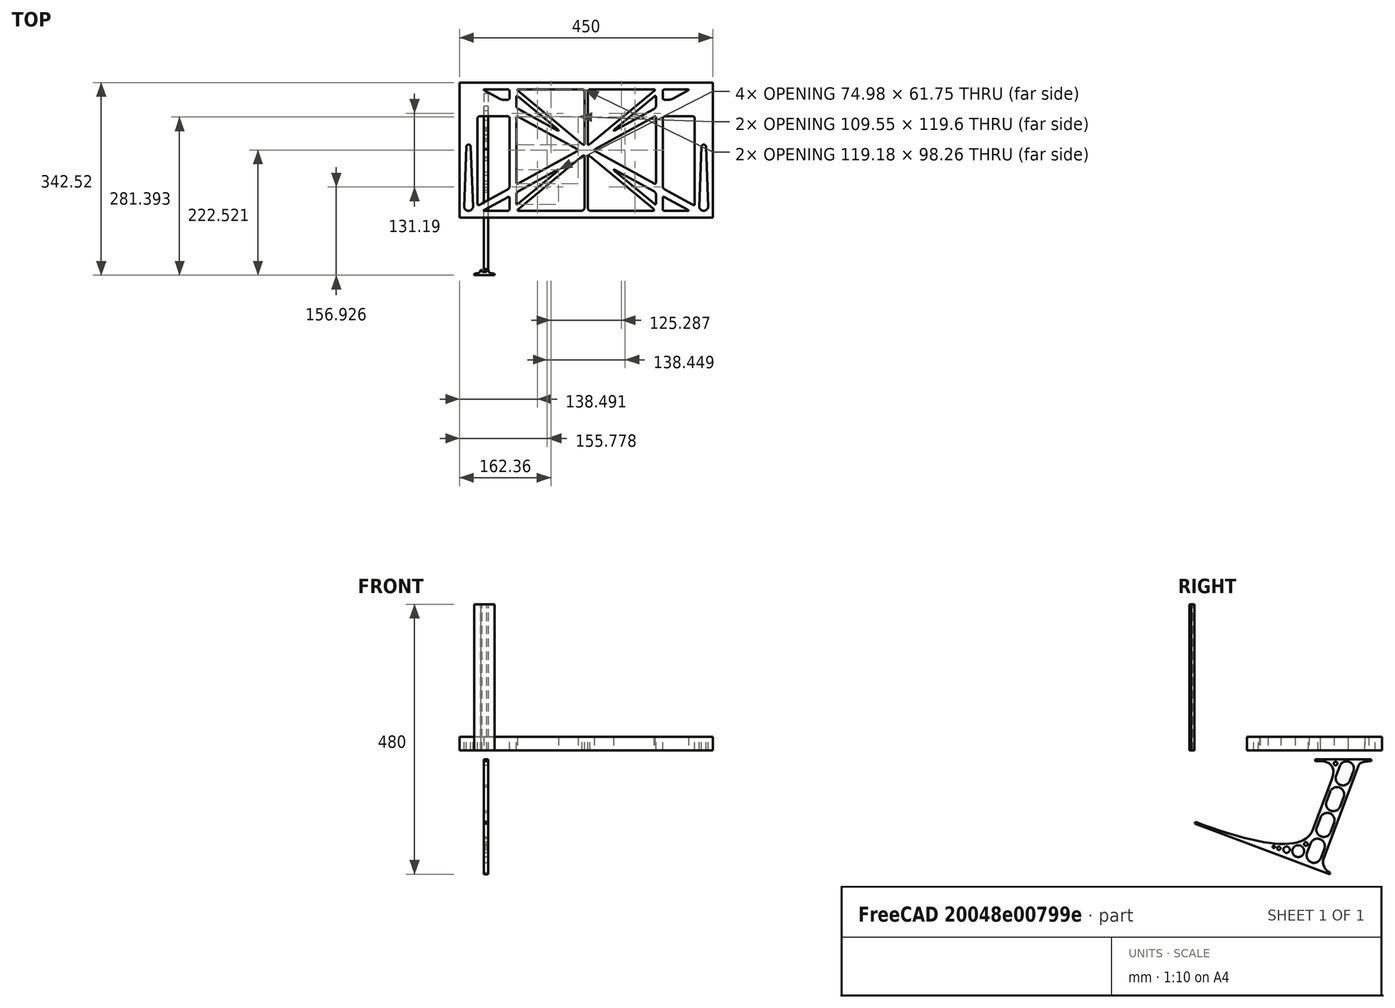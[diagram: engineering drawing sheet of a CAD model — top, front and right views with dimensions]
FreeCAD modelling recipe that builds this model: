
FCSTD DOCUMENT  (FreeCAD 0.19R0.19.2)
Label: laptopStand156FCStd
License: All rights reserved
LicenseURL: http://en.wikipedia.org/wiki/All_rights_reserved
objects: Sketcher::SketchObject×4, Part::Extrusion×3
note: 7 computed .brp shape members not serialized (recipe doc carries the construction recipe); baked Part::Feature solids carry a one-line shape summary decoded from their .brp

FEATURE [Sketcher::SketchObject] Sketch
  FullyConstrained = false
  sketch-geometry (349):
    g0: LineSegment StartX=-10.9272 StartY=-82.7794 StartZ=0 EndX=46.0728 EndY=-51.4823 EndZ=0
    g1: LineSegment StartX=-10.9272 StartY=76.4095 StartZ=0 EndX=-10.9272 EndY=-82.7794 EndZ=0
    g2: LineSegment StartX=46.0728 StartY=76.4095 StartZ=0 EndX=46.0728 EndY=-51.4823 EndZ=0
    g3: LineSegment StartX=-42.9272 StartY=136.221 StartZ=0 EndX=-42.9272 EndY=-103.779 EndZ=0
    g4: LineSegment StartX=407.073 StartY=136.221 StartZ=0 EndX=407.073 EndY=-103.779 EndZ=0
    g5: ArcOfCircle CenterX=-26.9272 CenterY=-83.7794 CenterZ=0 NormalX=0 NormalY=0 NormalZ=1 AngleXU=0 Radius=8 StartAngle=3.14159 EndAngle=6.28319
    g6: ArcOfCircle CenterX=391.073 CenterY=22.1087 CenterZ=0 NormalX=0 NormalY=0 NormalZ=1 AngleXU=0 Radius=8 StartAngle=-4.4e-15 EndAngle=3.14159
    g7: LineSegment StartX=399.073 StartY=22.1087 StartZ=0 EndX=399.073 EndY=-83.7794 EndZ=0
    g8: LineSegment StartX=383.073 StartY=22.1087 StartZ=0 EndX=383.073 EndY=-83.7794 EndZ=0
    g9: ArcOfCircle CenterX=391.073 CenterY=-83.7794 CenterZ=0 NormalX=0 NormalY=0 NormalZ=1 AngleXU=0 Radius=8 StartAngle=3.14159 EndAngle=6.28319
    g10: Circle CenterX=175.022 CenterY=27.0628 CenterZ=0 NormalX=0 NormalY=0 NormalZ=1 AngleXU=0 Radius=1
    g11: Circle CenterX=179.022 CenterY=24.8665 CenterZ=0 NormalX=0 NormalY=0 NormalZ=1 AngleXU=0 Radius=1
    g12: Circle CenterX=179.022 CenterY=27.0628 CenterZ=0 NormalX=0 NormalY=0 NormalZ=1 AngleXU=0 Radius=1
    g13: BSplineCurve PolesCount=3 KnotsCount=2 Degree=2 IsPeriodic=0
    g14: GeomPoint X=175.022 Y=27.0628 Z=0
    g15: GeomPoint X=179.022 Y=27.0628 Z=0
    g16: Circle CenterX=189.124 CenterY=27.0628 CenterZ=0 NormalX=0 NormalY=0 NormalZ=1 AngleXU=0 Radius=1
    g17: Circle CenterX=185.124 CenterY=24.8665 CenterZ=0 NormalX=0 NormalY=0 NormalZ=1 AngleXU=0 Radius=1
    g18: Circle CenterX=185.124 CenterY=27.0628 CenterZ=0 NormalX=0 NormalY=0 NormalZ=1 AngleXU=0 Radius=1
    g19: BSplineCurve PolesCount=3 KnotsCount=2 Degree=2 IsPeriodic=0
    g20: GeomPoint X=189.124 Y=27.0628 Z=0
    g21: GeomPoint X=185.124 Y=27.0628 Z=0
    g22: Circle CenterX=175.022 CenterY=5.37834 CenterZ=0 NormalX=0 NormalY=0 NormalZ=1 AngleXU=0 Radius=1
    g23: Circle CenterX=179.022 CenterY=7.57463 CenterZ=0 NormalX=0 NormalY=0 NormalZ=1 AngleXU=0 Radius=1
    g24: Circle CenterX=179.022 CenterY=5.34704 CenterZ=0 NormalX=0 NormalY=0 NormalZ=1 AngleXU=0 Radius=1
    g25: BSplineCurve PolesCount=3 KnotsCount=2 Degree=2 IsPeriodic=0
    g26: GeomPoint X=175.022 Y=5.37834 Z=0
    g27: GeomPoint X=179.022 Y=5.34704 Z=0
    g28: Circle CenterX=189.124 CenterY=5.37834 CenterZ=0 NormalX=0 NormalY=0 NormalZ=1 AngleXU=0 Radius=1
    g29: Circle CenterX=185.124 CenterY=7.57463 CenterZ=0 NormalX=0 NormalY=0 NormalZ=1 AngleXU=0 Radius=1
    g30: Circle CenterX=185.124 CenterY=5.34704 CenterZ=0 NormalX=0 NormalY=0 NormalZ=1 AngleXU=0 Radius=1
    g31: BSplineCurve PolesCount=3 KnotsCount=2 Degree=2 IsPeriodic=0
    g32: GeomPoint X=189.124 Y=5.37834 Z=0
    g33: GeomPoint X=185.124 Y=5.34704 Z=0
    g34: Circle CenterX=165.871 CenterY=18.1458 CenterZ=0 NormalX=0 NormalY=0 NormalZ=1 AngleXU=0 Radius=1
    g35: Circle CenterX=169.377 CenterY=16.2206 CenterZ=0 NormalX=0 NormalY=0 NormalZ=1 AngleXU=0 Radius=1
    g36: Circle CenterX=165.871 CenterY=14.2954 CenterZ=0 NormalX=0 NormalY=0 NormalZ=1 AngleXU=0 Radius=1
    g37: BSplineCurve PolesCount=3 KnotsCount=2 Degree=2 IsPeriodic=0
    g38: GeomPoint X=165.871 Y=18.1458 Z=0
    g39: GeomPoint X=165.871 Y=14.2954 Z=0
    g40: Circle CenterX=198.275 CenterY=18.1458 CenterZ=0 NormalX=0 NormalY=0 NormalZ=1 AngleXU=0 Radius=1
    g41: Circle CenterX=194.768 CenterY=16.2206 CenterZ=0 NormalX=0 NormalY=0 NormalZ=1 AngleXU=0 Radius=1
    g42: Circle CenterX=198.275 CenterY=14.2954 CenterZ=0 NormalX=0 NormalY=0 NormalZ=1 AngleXU=0 Radius=1
    g43: BSplineCurve PolesCount=3 KnotsCount=2 Degree=2 IsPeriodic=0
    g44: GeomPoint X=198.275 Y=18.1458 Z=0
    g45: GeomPoint X=198.275 Y=14.2954 Z=0
    g46: LineSegment StartX=407.073 StartY=-103.779 StartZ=0 EndX=-42.9272 EndY=-103.779 EndZ=0
    g47: LineSegment StartX=407.073 StartY=136.221 StartZ=0 EndX=-42.9272 EndY=136.221 EndZ=0
    g48: LineSegment StartX=46.0728 StartY=76.4095 StartZ=0 EndX=-10.9272 EndY=76.4095 EndZ=0
    g49: Circle CenterX=125.607 CenterY=54.1951 CenterZ=0 NormalX=0 NormalY=0 NormalZ=1 AngleXU=0 Radius=1
    g50: Circle CenterX=139.632 CenterY=46.4944 CenterZ=0 NormalX=0 NormalY=0 NormalZ=1 AngleXU=0 Radius=1
    g51: Circle CenterX=127.326 CenterY=56.7187 CenterZ=0 NormalX=0 NormalY=0 NormalZ=1 AngleXU=0 Radius=1
    g52: BSplineCurve PolesCount=3 KnotsCount=2 Degree=2 IsPeriodic=0
    g53: GeomPoint X=125.607 Y=54.1951 Z=0
    g54: GeomPoint X=127.326 Y=56.7187 Z=0
    g55: Circle CenterX=236.821 CenterY=56.7187 CenterZ=0 NormalX=0 NormalY=0 NormalZ=1 AngleXU=0 Radius=1
    g56: Circle CenterX=224.513 CenterY=46.4944 CenterZ=0 NormalX=0 NormalY=0 NormalZ=1 AngleXU=0 Radius=1
    g57: Circle CenterX=238.538 CenterY=54.1951 CenterZ=0 NormalX=0 NormalY=0 NormalZ=1 AngleXU=0 Radius=1
    g58: BSplineCurve PolesCount=3 KnotsCount=2 Degree=2 IsPeriodic=0
    g59: GeomPoint X=236.821 Y=56.7187 Z=0
    g60: GeomPoint X=238.538 Y=54.1951 Z=0
    g61: Circle CenterX=238.538 CenterY=-21.7539 CenterZ=0 NormalX=0 NormalY=0 NormalZ=1 AngleXU=0 Radius=1
    g62: Circle CenterX=224.513 CenterY=-14.0532 CenterZ=0 NormalX=0 NormalY=0 NormalZ=1 AngleXU=0 Radius=1
    g63: Circle CenterX=236.821 CenterY=-24.2775 CenterZ=0 NormalX=0 NormalY=0 NormalZ=1 AngleXU=0 Radius=1
    g64: BSplineCurve PolesCount=3 KnotsCount=2 Degree=2 IsPeriodic=0
    g65: GeomPoint X=238.538 Y=-21.7539 Z=0
    g66: GeomPoint X=236.821 Y=-24.2775 Z=0
    g67: Circle CenterX=125.607 CenterY=-21.7539 CenterZ=0 NormalX=0 NormalY=0 NormalZ=1 AngleXU=0 Radius=1
    g68: Circle CenterX=139.632 CenterY=-14.0532 CenterZ=0 NormalX=0 NormalY=0 NormalZ=1 AngleXU=0 Radius=1
    g69: Circle CenterX=127.325 CenterY=-24.2775 CenterZ=0 NormalX=0 NormalY=0 NormalZ=1 AngleXU=0 Radius=1
    g70: BSplineCurve PolesCount=3 KnotsCount=2 Degree=2 IsPeriodic=0
    g71: GeomPoint X=125.607 Y=-21.7539 Z=0
    g72: GeomPoint X=127.325 Y=-24.2775 Z=0
    g73: Circle CenterX=302.996 CenterY=111.695 CenterZ=0 NormalX=0 NormalY=0 NormalZ=1 AngleXU=0 Radius=1
    g74: Circle CenterX=306.073 CenterY=114.251 CenterZ=0 NormalX=0 NormalY=0 NormalZ=1 AngleXU=0 Radius=1
    g75: Circle CenterX=306.073 CenterY=110.251 CenterZ=0 NormalX=0 NormalY=0 NormalZ=1 AngleXU=0 Radius=1
    g76: BSplineCurve PolesCount=3 KnotsCount=2 Degree=2 IsPeriodic=0
    g77: GeomPoint X=302.996 Y=111.695 Z=0
    g78: GeomPoint X=306.073 Y=110.251 Z=0
    g79: Circle CenterX=306.073 CenterY=95.2763 CenterZ=0 NormalX=0 NormalY=0 NormalZ=1 AngleXU=0 Radius=1
    g80: Circle CenterX=306.073 CenterY=91.2763 CenterZ=0 NormalX=0 NormalY=0 NormalZ=1 AngleXU=0 Radius=1
    g81: Circle CenterX=302.567 CenterY=89.3511 CenterZ=0 NormalX=0 NormalY=0 NormalZ=1 AngleXU=0 Radius=1
    g82: BSplineCurve PolesCount=3 KnotsCount=2 Degree=2 IsPeriodic=0
    g83: GeomPoint X=306.073 Y=95.2763 Z=0
    g84: GeomPoint X=302.567 Y=89.3511 Z=0
    g85: LineSegment StartX=306.073 StartY=110.251 StartZ=0 EndX=306.073 EndY=95.2763 EndZ=0
    g86: LineSegment StartX=302.996 StartY=111.695 StartZ=0 EndX=236.821 EndY=56.7187 EndZ=0
    g87: LineSegment StartX=238.538 StartY=54.1951 StartZ=0 EndX=302.567 EndY=89.3511 EndZ=0
    g88: Circle CenterX=61.1496 CenterY=111.695 CenterZ=0 NormalX=0 NormalY=0 NormalZ=1 AngleXU=0 Radius=1
    g89: Circle CenterX=58.0728 CenterY=114.251 CenterZ=0 NormalX=0 NormalY=0 NormalZ=1 AngleXU=0 Radius=1
    g90: Circle CenterX=58.0728 CenterY=110.251 CenterZ=0 NormalX=0 NormalY=0 NormalZ=1 AngleXU=0 Radius=1
    g91: BSplineCurve PolesCount=3 KnotsCount=2 Degree=2 IsPeriodic=0
    g92: GeomPoint X=61.1496 Y=111.695 Z=0
    g93: GeomPoint X=58.0728 Y=110.251 Z=0
    g94: Circle CenterX=61.5791 CenterY=89.3511 CenterZ=0 NormalX=0 NormalY=0 NormalZ=1 AngleXU=0 Radius=1
    g95: Circle CenterX=58.0728 CenterY=91.2763 CenterZ=0 NormalX=0 NormalY=0 NormalZ=1 AngleXU=0 Radius=1
    g96: Circle CenterX=58.0728 CenterY=95.2763 CenterZ=0 NormalX=0 NormalY=0 NormalZ=1 AngleXU=0 Radius=1
    g97: BSplineCurve PolesCount=3 KnotsCount=2 Degree=2 IsPeriodic=0
    g98: GeomPoint X=61.5791 Y=89.3511 Z=0
    g99: GeomPoint X=58.0728 Y=95.2763 Z=0
    g100: LineSegment StartX=58.0728 StartY=110.251 StartZ=0 EndX=58.0728 EndY=95.2763 EndZ=0
    g101: LineSegment StartX=61.1496 StartY=111.695 StartZ=0 EndX=127.326 EndY=56.7187 EndZ=0
    g102: LineSegment StartX=125.607 StartY=54.1951 StartZ=0 EndX=61.5791 EndY=89.3511 EndZ=0
    g103: Circle CenterX=61.5791 CenterY=-56.9099 CenterZ=0 NormalX=0 NormalY=0 NormalZ=1 AngleXU=0 Radius=1
    g104: Circle CenterX=58.0728 CenterY=-58.8351 CenterZ=0 NormalX=0 NormalY=0 NormalZ=1 AngleXU=0 Radius=1
    g105: Circle CenterX=58.0728 CenterY=-62.8351 CenterZ=0 NormalX=0 NormalY=0 NormalZ=1 AngleXU=0 Radius=1
    g106: BSplineCurve PolesCount=3 KnotsCount=2 Degree=2 IsPeriodic=0
    g107: GeomPoint X=61.5791 Y=-56.9099 Z=0
    g108: GeomPoint X=58.0728 Y=-62.8351 Z=0
    g109: Circle CenterX=58.0728 CenterY=-77.8102 CenterZ=0 NormalX=0 NormalY=0 NormalZ=1 AngleXU=0 Radius=1
    g110: Circle CenterX=58.0728 CenterY=-81.8102 CenterZ=0 NormalX=0 NormalY=0 NormalZ=1 AngleXU=0 Radius=1
    g111: Circle CenterX=61.1496 CenterY=-79.2541 CenterZ=0 NormalX=0 NormalY=0 NormalZ=1 AngleXU=0 Radius=1
    g112: BSplineCurve PolesCount=3 KnotsCount=2 Degree=2 IsPeriodic=0
    g113: GeomPoint X=58.0728 Y=-77.8102 Z=0
    g114: GeomPoint X=61.1496 Y=-79.2541 Z=0
    g115: LineSegment StartX=58.0728 StartY=-62.8351 StartZ=0 EndX=58.0728 EndY=-77.8102 EndZ=0
    g116: LineSegment StartX=61.1496 StartY=-79.2541 StartZ=0 EndX=127.325 EndY=-24.2775 EndZ=0
    g117: LineSegment StartX=125.607 StartY=-21.7539 StartZ=0 EndX=61.5791 EndY=-56.9099 EndZ=0
    g118: Circle CenterX=302.567 CenterY=-56.9099 CenterZ=0 NormalX=0 NormalY=0 NormalZ=1 AngleXU=0 Radius=1
    g119: Circle CenterX=306.073 CenterY=-58.8351 CenterZ=0 NormalX=0 NormalY=0 NormalZ=1 AngleXU=0 Radius=1
    g120: Circle CenterX=306.073 CenterY=-62.8351 CenterZ=0 NormalX=0 NormalY=0 NormalZ=1 AngleXU=0 Radius=1
    g121: BSplineCurve PolesCount=3 KnotsCount=2 Degree=2 IsPeriodic=0
    g122: GeomPoint X=302.567 Y=-56.9099 Z=0
    g123: GeomPoint X=306.073 Y=-62.8351 Z=0
    g124: Circle CenterX=302.996 CenterY=-79.2541 CenterZ=0 NormalX=0 NormalY=0 NormalZ=1 AngleXU=0 Radius=1
    g125: Circle CenterX=306.073 CenterY=-81.8102 CenterZ=0 NormalX=0 NormalY=0 NormalZ=1 AngleXU=0 Radius=1
    g126: Circle CenterX=306.073 CenterY=-77.8102 CenterZ=0 NormalX=0 NormalY=0 NormalZ=1 AngleXU=0 Radius=1
    g127: BSplineCurve PolesCount=3 KnotsCount=2 Degree=2 IsPeriodic=0
    g128: GeomPoint X=302.996 Y=-79.2541 Z=0
    g129: GeomPoint X=306.073 Y=-77.8102 Z=0
    g130: LineSegment StartX=306.073 StartY=-62.8351 StartZ=0 EndX=306.073 EndY=-77.8102 EndZ=0
    g131: LineSegment StartX=302.996 StartY=-79.2541 StartZ=0 EndX=236.821 EndY=-24.2775 EndZ=0
    g132: LineSegment StartX=238.538 StartY=-21.7539 StartZ=0 EndX=302.567 EndY=-56.9099 EndZ=0
    g133: Circle CenterX=61.6457 CenterY=-88.8112 CenterZ=0 NormalX=0 NormalY=0 NormalZ=1 AngleXU=0 Radius=1
    g134: Circle CenterX=58.0728 CenterY=-91.7794 CenterZ=0 NormalX=0 NormalY=0 NormalZ=1 AngleXU=0 Radius=1
    g135: Circle CenterX=63.9135 CenterY=-91.7794 CenterZ=0 NormalX=0 NormalY=0 NormalZ=1 AngleXU=0 Radius=1
    g136: BSplineCurve PolesCount=3 KnotsCount=2 Degree=2 IsPeriodic=0
    g137: GeomPoint X=61.6457 Y=-88.8112 Z=0
    g138: GeomPoint X=63.9135 Y=-91.7794 Z=0
    g139: Circle CenterX=179.022 CenterY=-85.8163 CenterZ=0 NormalX=0 NormalY=0 NormalZ=1 AngleXU=0 Radius=1
    g140: Circle CenterX=179.022 CenterY=-91.7794 CenterZ=0 NormalX=0 NormalY=0 NormalZ=1 AngleXU=0 Radius=1
    g141: Circle CenterX=171.895 CenterY=-91.7794 CenterZ=0 NormalX=0 NormalY=0 NormalZ=1 AngleXU=0 Radius=1
    g142: BSplineCurve PolesCount=3 KnotsCount=2 Degree=2 IsPeriodic=0
    g143: GeomPoint X=179.022 Y=-85.8163 Z=0
    g144: GeomPoint X=171.895 Y=-91.7794 Z=0
    g145: Circle CenterX=185.124 CenterY=-86.2028 CenterZ=0 NormalX=0 NormalY=0 NormalZ=1 AngleXU=0 Radius=1
    g146: Circle CenterX=185.124 CenterY=-91.7794 CenterZ=0 NormalX=0 NormalY=0 NormalZ=1 AngleXU=0 Radius=1
    g147: Circle CenterX=191.747 CenterY=-91.7794 CenterZ=0 NormalX=0 NormalY=0 NormalZ=1 AngleXU=0 Radius=1
    g148: BSplineCurve PolesCount=3 KnotsCount=2 Degree=2 IsPeriodic=0
    g149: GeomPoint X=185.124 Y=-86.2028 Z=0
    g150: GeomPoint X=191.747 Y=-91.7794 Z=0
    g151: Circle CenterX=299.888 CenterY=-86.6413 CenterZ=0 NormalX=0 NormalY=0 NormalZ=1 AngleXU=0 Radius=1
    g152: Circle CenterX=306.073 CenterY=-91.7794 CenterZ=0 NormalX=0 NormalY=0 NormalZ=1 AngleXU=0 Radius=1
    g153: Circle CenterX=298.776 CenterY=-91.7794 CenterZ=0 NormalX=0 NormalY=0 NormalZ=1 AngleXU=0 Radius=1
    g154: BSplineCurve PolesCount=3 KnotsCount=2 Degree=2 IsPeriodic=0
    g155: GeomPoint X=299.888 Y=-86.6413 Z=0
    g156: GeomPoint X=298.776 Y=-91.7794 Z=0
    g157: LineSegment StartX=189.124 StartY=5.37834 StartZ=0 EndX=299.888 EndY=-86.6413 EndZ=0
    g158: LineSegment StartX=298.776 StartY=-91.7794 StartZ=0 EndX=191.747 EndY=-91.7794 EndZ=0
    g159: LineSegment StartX=185.124 StartY=-86.2028 StartZ=0 EndX=185.124 EndY=5.34704 EndZ=0
    g160: LineSegment StartX=179.022 StartY=5.34704 StartZ=0 EndX=179.022 EndY=-85.8163 EndZ=0
    g161: LineSegment StartX=171.895 StartY=-91.7794 StartZ=0 EndX=63.9135 EndY=-91.7794 EndZ=0
    g162: LineSegment StartX=61.6457 StartY=-88.8112 StartZ=0 EndX=175.022 EndY=5.37834 EndZ=0
    g163: Circle CenterX=302.073 CenterY=124.221 CenterZ=0 NormalX=0 NormalY=0 NormalZ=1 AngleXU=0 Radius=1
    g164: Circle CenterX=306.073 CenterY=124.221 CenterZ=0 NormalX=0 NormalY=0 NormalZ=1 AngleXU=0 Radius=1
    g165: Circle CenterX=302.996 CenterY=121.665 CenterZ=0 NormalX=0 NormalY=0 NormalZ=1 AngleXU=0 Radius=1
    g166: BSplineCurve PolesCount=3 KnotsCount=2 Degree=2 IsPeriodic=0
    g167: GeomPoint X=302.073 Y=124.221 Z=0
    g168: GeomPoint X=302.996 Y=121.665 Z=0
    g169: Circle CenterX=189.124 CenterY=124.221 CenterZ=0 NormalX=0 NormalY=0 NormalZ=1 AngleXU=0 Radius=1
    g170: Circle CenterX=185.124 CenterY=124.221 CenterZ=0 NormalX=0 NormalY=0 NormalZ=1 AngleXU=0 Radius=1
    g171: Circle CenterX=185.124 CenterY=120.221 CenterZ=0 NormalX=0 NormalY=0 NormalZ=1 AngleXU=0 Radius=1
    g172: BSplineCurve PolesCount=3 KnotsCount=2 Degree=2 IsPeriodic=0
    g173: GeomPoint X=189.124 Y=124.221 Z=0
    g174: GeomPoint X=185.124 Y=120.221 Z=0
    g175: Circle CenterX=175.022 CenterY=124.221 CenterZ=0 NormalX=0 NormalY=0 NormalZ=1 AngleXU=0 Radius=1
    g176: Circle CenterX=179.022 CenterY=124.221 CenterZ=0 NormalX=0 NormalY=0 NormalZ=1 AngleXU=0 Radius=1
    g177: Circle CenterX=179.022 CenterY=120.221 CenterZ=0 NormalX=0 NormalY=0 NormalZ=1 AngleXU=0 Radius=1
    g178: BSplineCurve PolesCount=3 KnotsCount=2 Degree=2 IsPeriodic=0
    g179: GeomPoint X=175.022 Y=124.221 Z=0
    g180: GeomPoint X=179.022 Y=120.221 Z=0
    g181: Circle CenterX=62.0728 CenterY=124.221 CenterZ=0 NormalX=0 NormalY=0 NormalZ=1 AngleXU=0 Radius=1
    g182: Circle CenterX=58.0728 CenterY=124.221 CenterZ=0 NormalX=0 NormalY=0 NormalZ=1 AngleXU=0 Radius=1
    g183: Circle CenterX=61.1496 CenterY=121.665 CenterZ=0 NormalX=0 NormalY=0 NormalZ=1 AngleXU=0 Radius=1
    g184: BSplineCurve PolesCount=3 KnotsCount=2 Degree=2 IsPeriodic=0
    g185: GeomPoint X=62.0728 Y=124.221 Z=0
    g186: GeomPoint X=61.1496 Y=121.665 Z=0
    g187: LineSegment StartX=62.0728 StartY=124.221 StartZ=0 EndX=175.022 EndY=124.221 EndZ=0
    g188: LineSegment StartX=179.022 StartY=120.221 StartZ=0 EndX=179.022 EndY=27.0628 EndZ=0
    g189: LineSegment StartX=185.124 StartY=27.0628 StartZ=0 EndX=185.124 EndY=120.221 EndZ=0
    g190: LineSegment StartX=189.124 StartY=124.221 StartZ=0 EndX=302.073 EndY=124.221 EndZ=0
    g191: LineSegment StartX=302.996 StartY=121.665 StartZ=0 EndX=189.124 EndY=27.0628 EndZ=0
    g192: LineSegment StartX=175.022 StartY=27.0628 StartZ=0 EndX=61.1496 EndY=121.665 EndZ=0
    g193: Circle CenterX=61.5791 CenterY=75.4095 CenterZ=0 NormalX=0 NormalY=0 NormalZ=1 AngleXU=0 Radius=1
    g194: Circle CenterX=58.0728 CenterY=77.3346 CenterZ=0 NormalX=0 NormalY=0 NormalZ=1 AngleXU=0 Radius=1
    g195: Circle CenterX=58.0728 CenterY=73.3346 CenterZ=0 NormalX=0 NormalY=0 NormalZ=1 AngleXU=0 Radius=1
    g196: BSplineCurve PolesCount=3 KnotsCount=2 Degree=2 IsPeriodic=0
    g197: GeomPoint X=61.5791 Y=75.4095 Z=0
    g198: GeomPoint X=58.0728 Y=73.3346 Z=0
    g199: Circle CenterX=58.0728 CenterY=-40.8935 CenterZ=0 NormalX=0 NormalY=0 NormalZ=1 AngleXU=0 Radius=1
    g200: Circle CenterX=58.0728 CenterY=-44.8935 CenterZ=0 NormalX=0 NormalY=0 NormalZ=1 AngleXU=0 Radius=1
    g201: Circle CenterX=61.5791 CenterY=-42.9683 CenterZ=0 NormalX=0 NormalY=0 NormalZ=1 AngleXU=0 Radius=1
    g202: BSplineCurve PolesCount=3 KnotsCount=2 Degree=2 IsPeriodic=0
    g203: GeomPoint X=58.0728 Y=-40.8935 Z=0
    g204: GeomPoint X=61.5791 Y=-42.9683 Z=0
    g205: LineSegment StartX=61.5791 StartY=-42.9683 StartZ=0 EndX=165.871 EndY=14.2954 EndZ=0
    g206: LineSegment StartX=165.871 StartY=18.1458 StartZ=0 EndX=61.5791 EndY=75.4095 EndZ=0
    g207: LineSegment StartX=58.0728 StartY=73.3346 StartZ=0 EndX=58.0728 EndY=-40.8935 EndZ=0
    g208: Circle CenterX=302.567 CenterY=-42.9683 CenterZ=0 NormalX=0 NormalY=0 NormalZ=1 AngleXU=0 Radius=1
    g209: Circle CenterX=306.073 CenterY=-44.8935 CenterZ=0 NormalX=0 NormalY=0 NormalZ=1 AngleXU=0 Radius=1
    g210: Circle CenterX=306.073 CenterY=-40.8935 CenterZ=0 NormalX=0 NormalY=0 NormalZ=1 AngleXU=0 Radius=1
    g211: BSplineCurve PolesCount=3 KnotsCount=2 Degree=2 IsPeriodic=0
    g212: GeomPoint X=302.567 Y=-42.9683 Z=0
    g213: GeomPoint X=306.073 Y=-40.8935 Z=0
    g214: Circle CenterX=306.073 CenterY=73.3346 CenterZ=0 NormalX=0 NormalY=0 NormalZ=1 AngleXU=0 Radius=1
    g215: Circle CenterX=306.073 CenterY=77.3346 CenterZ=0 NormalX=0 NormalY=0 NormalZ=1 AngleXU=0 Radius=1
    g216: Circle CenterX=302.567 CenterY=75.4095 CenterZ=0 NormalX=0 NormalY=0 NormalZ=1 AngleXU=0 Radius=1
    g217: BSplineCurve PolesCount=3 KnotsCount=2 Degree=2 IsPeriodic=0
    g218: GeomPoint X=306.073 Y=73.3346 Z=0
    g219: GeomPoint X=302.567 Y=75.4095 Z=0
    g220: LineSegment StartX=302.567 StartY=-42.9683 StartZ=0 EndX=198.275 EndY=14.2954 EndZ=0
    g221: LineSegment StartX=198.275 StartY=18.1458 StartZ=0 EndX=302.567 EndY=75.4095 EndZ=0
    g222: LineSegment StartX=306.073 StartY=73.3346 StartZ=0 EndX=306.073 EndY=-40.8935 EndZ=0
    g223: LineSegment StartX=322.073 StartY=105.865 StartZ=0 EndX=328.643 EndY=105.865 EndZ=0
    g224: LineSegment StartX=318.073 StartY=120.221 StartZ=0 EndX=318.073 EndY=109.865 EndZ=0
    g225: LineSegment StartX=336.157 StartY=107.779 StartZ=0 EndX=362.567 EndY=122.294 EndZ=0
    g226: Circle CenterX=362.073 CenterY=124.221 CenterZ=0 NormalX=0 NormalY=0 NormalZ=1 AngleXU=0 Radius=1
    g227: Circle CenterX=366.073 CenterY=124.221 CenterZ=0 NormalX=0 NormalY=0 NormalZ=1 AngleXU=0 Radius=1
    g228: Circle CenterX=362.567 CenterY=122.294 CenterZ=0 NormalX=0 NormalY=0 NormalZ=1 AngleXU=0 Radius=1
    g229: BSplineCurve PolesCount=3 KnotsCount=2 Degree=2 IsPeriodic=0
    g230: GeomPoint X=362.073 Y=124.221 Z=0
    g231: GeomPoint X=362.567 Y=122.294 Z=0
    g232: Circle CenterX=322.073 CenterY=124.221 CenterZ=0 NormalX=0 NormalY=0 NormalZ=1 AngleXU=0 Radius=1
    g233: Circle CenterX=318.073 CenterY=124.221 CenterZ=0 NormalX=0 NormalY=0 NormalZ=1 AngleXU=0 Radius=1
    g234: Circle CenterX=318.073 CenterY=120.221 CenterZ=0 NormalX=0 NormalY=0 NormalZ=1 AngleXU=0 Radius=1
    g235: BSplineCurve PolesCount=3 KnotsCount=2 Degree=2 IsPeriodic=0
    g236: GeomPoint X=322.073 Y=124.221 Z=0
    g237: GeomPoint X=318.073 Y=120.221 Z=0
    g238: Circle CenterX=322.073 CenterY=105.865 CenterZ=0 NormalX=0 NormalY=0 NormalZ=1 AngleXU=0 Radius=1
    g239: Circle CenterX=318.073 CenterY=105.865 CenterZ=0 NormalX=0 NormalY=0 NormalZ=1 AngleXU=0 Radius=1
    g240: Circle CenterX=318.073 CenterY=109.865 CenterZ=0 NormalX=0 NormalY=0 NormalZ=1 AngleXU=0 Radius=1
    g241: BSplineCurve PolesCount=3 KnotsCount=2 Degree=2 IsPeriodic=0
    g242: GeomPoint X=322.073 Y=105.865 Z=0
    g243: GeomPoint X=318.073 Y=109.865 Z=0
    g244: Circle CenterX=336.157 CenterY=107.779 CenterZ=0 NormalX=0 NormalY=0 NormalZ=1 AngleXU=0 Radius=1
    g245: Circle CenterX=332.651 CenterY=105.853 CenterZ=0 NormalX=0 NormalY=0 NormalZ=1 AngleXU=0 Radius=1
    g246: Circle CenterX=328.643 CenterY=105.865 CenterZ=0 NormalX=0 NormalY=0 NormalZ=1 AngleXU=0 Radius=1
    g247: BSplineCurve PolesCount=3 KnotsCount=2 Degree=2 IsPeriodic=0
    g248: GeomPoint X=336.157 Y=107.779 Z=0
    g249: GeomPoint X=328.643 Y=105.865 Z=0
    g250: LineSegment StartX=322.073 StartY=124.221 StartZ=0 EndX=362.073 EndY=124.221 EndZ=0
    g251: Circle CenterX=371.567 CenterY=-80.8644 CenterZ=0 NormalX=0 NormalY=0 NormalZ=1 AngleXU=0 Radius=1
    g252: Circle CenterX=375.073 CenterY=-82.7896 CenterZ=0 NormalX=0 NormalY=0 NormalZ=1 AngleXU=0 Radius=1
    g253: Circle CenterX=375.073 CenterY=-78.7896 CenterZ=0 NormalX=0 NormalY=0 NormalZ=1 AngleXU=0 Radius=1
    g254: BSplineCurve PolesCount=3 KnotsCount=2 Degree=2 IsPeriodic=0
    g255: GeomPoint X=371.567 Y=-80.8644 Z=0
    g256: GeomPoint X=375.073 Y=-78.7896 Z=0
    g257: Circle CenterX=321.579 CenterY=-53.4075 CenterZ=0 NormalX=0 NormalY=0 NormalZ=1 AngleXU=0 Radius=1
    g258: Circle CenterX=318.073 CenterY=-51.4823 CenterZ=0 NormalX=0 NormalY=0 NormalZ=1 AngleXU=0 Radius=1
    g259: Circle CenterX=318.073 CenterY=-47.4805 CenterZ=0 NormalX=0 NormalY=0 NormalZ=1 AngleXU=0 Radius=1
    g260: BSplineCurve PolesCount=3 KnotsCount=2 Degree=2 IsPeriodic=0
    g261: GeomPoint X=321.579 Y=-53.4075 Z=0
    g262: GeomPoint X=318.073 Y=-47.4805 Z=0
    g263: LineSegment StartX=371.567 StartY=-80.8644 StartZ=0 EndX=321.579 EndY=-53.4075 EndZ=0
    g264: Circle CenterX=321.579 CenterY=-67.3492 CenterZ=0 NormalX=0 NormalY=0 NormalZ=1 AngleXU=0 Radius=1
    g265: Circle CenterX=318.073 CenterY=-65.424 CenterZ=0 NormalX=0 NormalY=0 NormalZ=1 AngleXU=0 Radius=1
    g266: Circle CenterX=318.073 CenterY=-69.424 CenterZ=0 NormalX=0 NormalY=0 NormalZ=1 AngleXU=0 Radius=1
    g267: BSplineCurve PolesCount=3 KnotsCount=2 Degree=2 IsPeriodic=0
    g268: GeomPoint X=321.579 Y=-67.3492 Z=0
    g269: GeomPoint X=318.073 Y=-69.424 Z=0
    g270: Circle CenterX=362.567 CenterY=-89.8542 CenterZ=0 NormalX=0 NormalY=0 NormalZ=1 AngleXU=0 Radius=1
    g271: Circle CenterX=366.073 CenterY=-91.7794 CenterZ=0 NormalX=0 NormalY=0 NormalZ=1 AngleXU=0 Radius=1
    g272: Circle CenterX=362.073 CenterY=-91.7794 CenterZ=0 NormalX=0 NormalY=0 NormalZ=1 AngleXU=0 Radius=1
    g273: BSplineCurve PolesCount=3 KnotsCount=2 Degree=2 IsPeriodic=0
    g274: GeomPoint X=362.567 Y=-89.8542 Z=0
    g275: GeomPoint X=362.073 Y=-91.7794 Z=0
    g276: Circle CenterX=322.073 CenterY=-91.7794 CenterZ=0 NormalX=0 NormalY=0 NormalZ=1 AngleXU=0 Radius=1
    g277: Circle CenterX=318.073 CenterY=-91.7794 CenterZ=0 NormalX=0 NormalY=0 NormalZ=1 AngleXU=0 Radius=1
    g278: Circle CenterX=318.073 CenterY=-87.7794 CenterZ=0 NormalX=0 NormalY=0 NormalZ=1 AngleXU=0 Radius=1
    g279: BSplineCurve PolesCount=3 KnotsCount=2 Degree=2 IsPeriodic=0
    g280: GeomPoint X=322.073 Y=-91.7794 Z=0
    g281: GeomPoint X=318.073 Y=-87.7794 Z=0
    g282: LineSegment StartX=362.567 StartY=-89.8542 StartZ=0 EndX=321.579 EndY=-67.3492 EndZ=0
    g283: LineSegment StartX=318.073 StartY=-69.424 StartZ=0 EndX=318.073 EndY=-87.7794 EndZ=0
    g284: LineSegment StartX=322.073 StartY=-91.7794 StartZ=0 EndX=362.073 EndY=-91.7794 EndZ=0
    g285: Circle CenterX=2.07281 CenterY=124.221 CenterZ=0 NormalX=0 NormalY=0 NormalZ=1 AngleXU=0 Radius=1
    g286: Circle CenterX=1.57905 CenterY=122.295 CenterZ=0 NormalX=0 NormalY=0 NormalZ=1 AngleXU=0 Radius=1
    g287: BSplineCurve PolesCount=3 KnotsCount=2 Degree=2 IsPeriodic=0
    g288: GeomPoint X=2.07281 Y=124.221 Z=0
    g289: GeomPoint X=1.57905 Y=122.295 Z=0
    g290: Circle CenterX=42.0728 CenterY=124.221 CenterZ=0 NormalX=0 NormalY=0 NormalZ=1 AngleXU=0 Radius=1
    g291: Circle CenterX=46.0728 CenterY=124.221 CenterZ=0 NormalX=0 NormalY=0 NormalZ=1 AngleXU=0 Radius=1
    g292: Circle CenterX=46.0728 CenterY=120.221 CenterZ=0 NormalX=0 NormalY=0 NormalZ=1 AngleXU=0 Radius=1
    g293: BSplineCurve PolesCount=3 KnotsCount=2 Degree=2 IsPeriodic=0
    g294: GeomPoint X=42.0728 Y=124.221 Z=0
    g295: GeomPoint X=46.0728 Y=120.221 Z=0
    g296: Circle CenterX=46.0728 CenterY=109.865 CenterZ=0 NormalX=0 NormalY=0 NormalZ=1 AngleXU=0 Radius=1
    g297: Circle CenterX=46.0728 CenterY=105.865 CenterZ=0 NormalX=0 NormalY=0 NormalZ=1 AngleXU=0 Radius=1
    g298: Circle CenterX=42.0728 CenterY=105.865 CenterZ=0 NormalX=0 NormalY=0 NormalZ=1 AngleXU=0 Radius=1
    g299: BSplineCurve PolesCount=3 KnotsCount=2 Degree=2 IsPeriodic=0
    g300: GeomPoint X=46.0728 Y=109.865 Z=0
    g301: GeomPoint X=42.0728 Y=105.865 Z=0
    g302: Circle CenterX=35.5028 CenterY=105.865 CenterZ=0 NormalX=0 NormalY=0 NormalZ=1 AngleXU=0 Radius=1
    g303: Circle CenterX=31.5028 CenterY=105.865 CenterZ=0 NormalX=0 NormalY=0 NormalZ=1 AngleXU=0 Radius=1
    g304: Circle CenterX=27.9965 CenterY=107.79 CenterZ=0 NormalX=0 NormalY=0 NormalZ=1 AngleXU=0 Radius=1
    g305: BSplineCurve PolesCount=3 KnotsCount=2 Degree=2 IsPeriodic=0
    g306: GeomPoint X=35.5028 Y=105.865 Z=0
    g307: GeomPoint X=27.9965 Y=107.79 Z=0
    g308: LineSegment StartX=2.07281 StartY=124.221 StartZ=0 EndX=42.0728 EndY=124.221 EndZ=0
    g309: LineSegment StartX=46.0728 StartY=120.221 StartZ=0 EndX=46.0728 EndY=109.865 EndZ=0
    g310: LineSegment StartX=42.0728 StartY=105.865 StartZ=0 EndX=35.5028 EndY=105.865 EndZ=0
    g311: LineSegment StartX=27.9965 StartY=107.79 StartZ=0 EndX=1.57905 EndY=122.295 EndZ=0
    g312: Circle CenterX=42.5666 CenterY=-67.3492 CenterZ=0 NormalX=0 NormalY=0 NormalZ=1 AngleXU=0 Radius=1
    g313: Circle CenterX=46.0728 CenterY=-65.424 CenterZ=0 NormalX=0 NormalY=0 NormalZ=1 AngleXU=0 Radius=1
    g314: Circle CenterX=46.0728 CenterY=-69.424 CenterZ=0 NormalX=0 NormalY=0 NormalZ=1 AngleXU=0 Radius=1
    g315: BSplineCurve PolesCount=3 KnotsCount=2 Degree=2 IsPeriodic=0
    g316: GeomPoint X=42.5666 Y=-67.3492 Z=0
    g317: GeomPoint X=46.0728 Y=-69.424 Z=0
    g318: Circle CenterX=46.0728 CenterY=-87.7794 CenterZ=0 NormalX=0 NormalY=0 NormalZ=1 AngleXU=0 Radius=1
    g319: Circle CenterX=46.0728 CenterY=-91.7794 CenterZ=0 NormalX=0 NormalY=0 NormalZ=1 AngleXU=0 Radius=1
    g320: Circle CenterX=42.0728 CenterY=-91.7794 CenterZ=0 NormalX=0 NormalY=0 NormalZ=1 AngleXU=0 Radius=1
    g321: BSplineCurve PolesCount=3 KnotsCount=2 Degree=2 IsPeriodic=0
    g322: GeomPoint X=46.0728 Y=-87.7794 Z=0
    g323: GeomPoint X=42.0728 Y=-91.7794 Z=0
    g324: Circle CenterX=2.07281 CenterY=-91.7794 CenterZ=0 NormalX=0 NormalY=0 NormalZ=1 AngleXU=0 Radius=1
    g325: Circle CenterX=-1.92719 CenterY=-91.7794 CenterZ=0 NormalX=0 NormalY=0 NormalZ=1 AngleXU=0 Radius=1
    g326: Circle CenterX=1.57905 CenterY=-89.8542 CenterZ=0 NormalX=0 NormalY=0 NormalZ=1 AngleXU=0 Radius=1
    g327: BSplineCurve PolesCount=3 KnotsCount=2 Degree=2 IsPeriodic=0
    g328: GeomPoint X=2.07281 Y=-91.7794 Z=0
    g329: GeomPoint X=1.57905 Y=-89.8542 Z=0
    g330: LineSegment StartX=2.07281 StartY=-91.7794 StartZ=0 EndX=42.0728 EndY=-91.7794 EndZ=0
    g331: LineSegment StartX=46.0728 StartY=-87.7794 StartZ=0 EndX=46.0728 EndY=-69.424 EndZ=0
    g332: LineSegment StartX=42.5666 StartY=-67.3492 StartZ=0 EndX=1.57905 EndY=-89.8542 EndZ=0
    g333: Circle CenterX=322.073 CenterY=76.4095 CenterZ=0 NormalX=0 NormalY=0 NormalZ=1 AngleXU=0 Radius=4
    g334: BSplineCurve PolesCount=3 KnotsCount=2 Degree=2 IsPeriodic=0
    g335: GeomPoint X=318.073 Y=72.4095 Z=0
    g336: GeomPoint X=322.073 Y=76.4095 Z=0
    g337: Circle CenterX=375.073 CenterY=72.4095 CenterZ=0 NormalX=0 NormalY=0 NormalZ=1 AngleXU=0 Radius=1
    g338: Circle CenterX=375.073 CenterY=76.4095 CenterZ=0 NormalX=0 NormalY=0 NormalZ=1 AngleXU=0 Radius=1
    g339: Circle CenterX=371.073 CenterY=76.4095 CenterZ=0 NormalX=0 NormalY=0 NormalZ=1 AngleXU=0 Radius=1
    g340: BSplineCurve PolesCount=3 KnotsCount=2 Degree=2 IsPeriodic=0
    g341: GeomPoint X=375.073 Y=72.4095 Z=0
    g342: GeomPoint X=371.073 Y=76.4095 Z=0
    g343: LineSegment StartX=322.073 StartY=76.4095 StartZ=0 EndX=371.073 EndY=76.4095 EndZ=0
    g344: LineSegment StartX=318.073 StartY=72.4095 StartZ=0 EndX=318.073 EndY=-47.4805 EndZ=0
    g345: LineSegment StartX=375.073 StartY=72.4095 StartZ=0 EndX=375.073 EndY=-78.7896 EndZ=0
    g346: ArcOfCircle CenterX=-26.9272 CenterY=22.1087 CenterZ=0 NormalX=0 NormalY=0 NormalZ=1 AngleXU=0 Radius=4 StartAngle=5e-16 EndAngle=3.14159
    g347: LineSegment StartX=-30.9272 StartY=22.1087 StartZ=0 EndX=-34.9272 EndY=-83.7794 EndZ=0
    g348: LineSegment StartX=-18.9272 StartY=-83.7794 StartZ=0 EndX=-22.9272 EndY=22.1087 EndZ=0
  constraints (572):
    c: Coincident(g0,g2)
    c: Block(g0)
    c: Block(g1)
    c: Vertical(g3)
    c: Vertical(g4)
    c: Block(g4)
    c: Block(g3)
    c: Tangent(g6,g7) = 1.5708
    c: Tangent(g7,g9) = 1.5708
    c: Equal(g6,g9)
    c: Coincident(g8,g6)
    c: Coincident(g8,g9)
    c: Block(g7)
    c: Block(g8)
    c: Weight(g10) = 1
    c: Equal(g10,g11)
    c: Equal(g10,g12)
    c: InternalAlignment(g10,g13)
    c: InternalAlignment(g11,g13)
    c: InternalAlignment(g12,g13)
    c: InternalAlignment(g14,g13)
    c: InternalAlignment(g15,g13)
    c: Weight(g16) = 1
    c: Equal(g16,g17)
    c: Equal(g16,g18)
    c: InternalAlignment(g16,g19)
    c: InternalAlignment(g17,g19)
    c: InternalAlignment(g18,g19)
    c: InternalAlignment(g20,g19)
    c: InternalAlignment(g21,g19)
    c: Block(g19)
    c: Block(g13)
    c: Weight(g22) = 1
    c: Equal(g22,g23)
    c: Equal(g22,g24)
    c: InternalAlignment(g22,g25)
    c: InternalAlignment(g23,g25)
    c: InternalAlignment(g24,g25)
    c: InternalAlignment(g26,g25)
    c: InternalAlignment(g27,g25)
    c: Weight(g28) = 1
    c: Equal(g28,g29)
    c: Equal(g28,g30)
    c: InternalAlignment(g28,g31)
    c: InternalAlignment(g29,g31)
    c: InternalAlignment(g30,g31)
    c: InternalAlignment(g32,g31)
    c: InternalAlignment(g33,g31)
    c: Block(g31)
    c: Block(g25)
    c: Weight(g34) = 1
    c: Equal(g34,g35)
    c: Equal(g34,g36)
    c: InternalAlignment(g34,g37)
    c: InternalAlignment(g35,g37)
    c: InternalAlignment(g36,g37)
    c: InternalAlignment(g38,g37)
    c: InternalAlignment(g39,g37)
    c: Weight(g40) = 1
    c: Equal(g40,g41)
    c: Equal(g40,g42)
    c: InternalAlignment(g40,g43)
    c: InternalAlignment(g41,g43)
    c: InternalAlignment(g42,g43)
    c: InternalAlignment(g44,g43)
    c: InternalAlignment(g45,g43)
    c: Block(g37)
    c: Block(g43)
    c: Coincident(g46,g4)
    c: Coincident(g46,g3)
    c: Horizontal(g46)
    c: Distance(g46) = 450
    c: Coincident(g47,g4)
    c: Coincident(g47,g3)
    c: Horizontal(g47)
    c: Horizontal(g48)
    c: Coincident(g2,g48)
    c: Block(g48)
    c: Coincident(g1,g48)
    c: Weight(g49) = 1
    c: Equal(g49,g50)
    c: Equal(g49,g51)
    c: InternalAlignment(g49,g52)
    c: InternalAlignment(g50,g52)
    c: InternalAlignment(g51,g52)
    c: InternalAlignment(g53,g52)
    c: InternalAlignment(g54,g52)
    c: Block(g52)
    c: Weight(g55) = 1
    c: Equal(g55,g56)
    c: Equal(g55,g57)
    c: InternalAlignment(g55,g58)
    c: InternalAlignment(g56,g58)
    c: InternalAlignment(g57,g58)
    c: InternalAlignment(g59,g58)
    c: InternalAlignment(g60,g58)
    c: Block(g58)
    c: Weight(g61) = 1
    c: Equal(g61,g62)
    c: Equal(g61,g63)
    c: InternalAlignment(g61,g64)
    c: InternalAlignment(g62,g64)
    c: InternalAlignment(g63,g64)
    c: InternalAlignment(g65,g64)
    c: InternalAlignment(g66,g64)
    c: Block(g64)
    c: Weight(g67) = 1
    c: Equal(g67,g68)
    c: Equal(g67,g69)
    c: InternalAlignment(g67,g70)
    c: InternalAlignment(g68,g70)
    c: InternalAlignment(g69,g70)
    c: InternalAlignment(g71,g70)
    c: InternalAlignment(g72,g70)
    c: Block(g70)
    c: Weight(g73) = 1
    c: Equal(g73,g74)
    c: Equal(g73,g75)
    c: InternalAlignment(g73,g76)
    c: InternalAlignment(g74,g76)
    c: InternalAlignment(g75,g76)
    c: InternalAlignment(g77,g76)
    c: InternalAlignment(g78,g76)
    c: Weight(g79) = 1
    c: Equal(g79,g80)
    c: Equal(g79,g81)
    c: InternalAlignment(g79,g82)
    c: InternalAlignment(g80,g82)
    c: InternalAlignment(g81,g82)
    c: InternalAlignment(g83,g82)
    c: InternalAlignment(g84,g82)
    c: Block(g76)
    c: Block(g82)
    c: Coincident(g85,g76)
    c: Coincident(g85,g82)
    c: Vertical(g85)
    c: Coincident(g86,g76)
    c: Coincident(g86,g58)
    c: Coincident(g87,g58)
    c: Coincident(g87,g82)
    c: Weight(g88) = 1
    c: Equal(g88,g89)
    c: Equal(g88,g90)
    c: InternalAlignment(g88,g91)
    c: InternalAlignment(g89,g91)
    c: InternalAlignment(g90,g91)
    c: InternalAlignment(g92,g91)
    c: InternalAlignment(g93,g91)
    c: Weight(g94) = 1
    c: Equal(g94,g95)
    c: Equal(g94,g96)
    c: InternalAlignment(g94,g97)
    c: InternalAlignment(g95,g97)
    c: InternalAlignment(g96,g97)
    c: InternalAlignment(g98,g97)
    c: InternalAlignment(g99,g97)
    c: Block(g91)
    c: Block(g97)
    c: Coincident(g100,g91)
    c: Coincident(g100,g97)
    c: Vertical(g100)
    c: Coincident(g101,g91)
    c: Coincident(g101,g52)
    c: Coincident(g102,g52)
    c: Coincident(g102,g97)
    c: Weight(g103) = 1
    c: Equal(g103,g104)
    c: Equal(g103,g105)
    c: InternalAlignment(g103,g106)
    c: InternalAlignment(g104,g106)
    c: InternalAlignment(g105,g106)
    c: InternalAlignment(g107,g106)
    c: InternalAlignment(g108,g106)
    c: Weight(g109) = 1
    c: Equal(g109,g110)
    c: Equal(g109,g111)
    c: InternalAlignment(g109,g112)
    c: InternalAlignment(g110,g112)
    c: InternalAlignment(g111,g112)
    c: InternalAlignment(g113,g112)
    c: InternalAlignment(g114,g112)
    c: Block(g106)
    c: Block(g112)
    c: Coincident(g115,g106)
    c: Coincident(g115,g112)
    c: Vertical(g115)
    c: Coincident(g116,g112)
    c: Coincident(g116,g70)
    c: Coincident(g117,g70)
    c: Coincident(g117,g106)
    c: Weight(g118) = 1
    c: Equal(g118,g119)
    c: Equal(g118,g120)
    c: InternalAlignment(g118,g121)
    c: InternalAlignment(g119,g121)
    c: InternalAlignment(g120,g121)
    c: InternalAlignment(g122,g121)
    c: InternalAlignment(g123,g121)
    c: Weight(g124) = 1
    c: Equal(g124,g125)
    c: Equal(g124,g126)
    c: InternalAlignment(g124,g127)
    c: InternalAlignment(g125,g127)
    c: InternalAlignment(g126,g127)
    c: InternalAlignment(g128,g127)
    c: InternalAlignment(g129,g127)
    c: Block(g121)
    c: Block(g127)
    c: Coincident(g130,g121)
    c: Coincident(g130,g127)
    c: Vertical(g130)
    c: Coincident(g131,g127)
    c: Coincident(g131,g64)
    c: Coincident(g132,g64)
    c: Coincident(g132,g121)
    c: Weight(g133) = 1
    c: Equal(g133,g134)
    c: Equal(g133,g135)
    c: InternalAlignment(g133,g136)
    c: InternalAlignment(g134,g136)
    c: InternalAlignment(g135,g136)
    c: InternalAlignment(g137,g136)
    c: InternalAlignment(g138,g136)
    c: Weight(g139) = 1
    c: Equal(g139,g140)
    c: Equal(g139,g141)
    c: InternalAlignment(g139,g142)
    c: InternalAlignment(g140,g142)
    c: InternalAlignment(g141,g142)
    c: InternalAlignment(g143,g142)
    c: InternalAlignment(g144,g142)
    c: Weight(g145) = 1
    c: Equal(g145,g146)
    c: Equal(g145,g147)
    c: InternalAlignment(g145,g148)
    c: InternalAlignment(g146,g148)
    c: InternalAlignment(g147,g148)
    c: InternalAlignment(g149,g148)
    c: InternalAlignment(g150,g148)
    c: Weight(g151) = 1
    c: Equal(g151,g152)
    c: Equal(g151,g153)
    c: InternalAlignment(g151,g154)
    c: InternalAlignment(g152,g154)
    c: InternalAlignment(g153,g154)
    c: InternalAlignment(g155,g154)
    c: InternalAlignment(g156,g154)
    c: Block(g154)
    c: Block(g148)
    c: Block(g142)
    c: Block(g136)
    c: Coincident(g157,g31)
    c: Coincident(g157,g154)
    c: Coincident(g158,g154)
    c: Coincident(g158,g148)
    c: Horizontal(g158)
    c: Coincident(g159,g148)
    c: Coincident(g159,g31)
    c: Vertical(g159)
    c: Coincident(g160,g25)
    c: Coincident(g160,g142)
    c: Vertical(g160)
    c: Coincident(g161,g142)
    c: Coincident(g161,g136)
    c: Horizontal(g161)
    c: Coincident(g162,g136)
    c: Coincident(g162,g25)
    c: Weight(g163) = 1
    c: Equal(g163,g164)
    c: Equal(g163,g165)
    c: InternalAlignment(g163,g166)
    c: InternalAlignment(g164,g166)
    c: InternalAlignment(g165,g166)
    c: InternalAlignment(g167,g166)
    c: InternalAlignment(g168,g166)
    c: Weight(g169) = 1
    c: Equal(g169,g170)
    c: Equal(g169,g171)
    c: InternalAlignment(g169,g172)
    c: InternalAlignment(g170,g172)
    c: InternalAlignment(g171,g172)
    c: InternalAlignment(g173,g172)
    c: InternalAlignment(g174,g172)
    c: Weight(g175) = 1
    c: Equal(g175,g176)
    c: Equal(g175,g177)
    c: InternalAlignment(g175,g178)
    c: InternalAlignment(g176,g178)
    c: InternalAlignment(g177,g178)
    c: InternalAlignment(g179,g178)
    c: InternalAlignment(g180,g178)
    c: Weight(g181) = 1
    c: Equal(g181,g182)
    c: Equal(g181,g183)
    c: InternalAlignment(g181,g184)
    c: InternalAlignment(g182,g184)
    c: InternalAlignment(g183,g184)
    c: InternalAlignment(g185,g184)
    c: InternalAlignment(g186,g184)
    c: Block(g184)
    c: Block(g178)
    c: Block(g172)
    c: Block(g166)
    c: Coincident(g187,g184)
    c: Coincident(g187,g178)
    c: Horizontal(g187)
    c: Coincident(g188,g178)
    c: Coincident(g188,g13)
    c: Vertical(g188)
    c: Coincident(g189,g19)
    c: Coincident(g189,g172)
    c: Vertical(g189)
    c: Coincident(g190,g172)
    c: Coincident(g190,g166)
    c: Horizontal(g190)
    c: Coincident(g191,g166)
    c: Coincident(g191,g19)
    c: Coincident(g192,g13)
    c: Weight(g193) = 1
    c: Equal(g193,g194)
    c: Equal(g193,g195)
    c: InternalAlignment(g193,g196)
    c: InternalAlignment(g194,g196)
    c: InternalAlignment(g195,g196)
    c: InternalAlignment(g197,g196)
    c: InternalAlignment(g198,g196)
    c: Weight(g199) = 1
    c: Equal(g199,g200)
    c: Equal(g199,g201)
    c: InternalAlignment(g199,g202)
    c: InternalAlignment(g200,g202)
    c: InternalAlignment(g201,g202)
    c: InternalAlignment(g203,g202)
    c: InternalAlignment(g204,g202)
    c: Block(g202)
    c: Block(g196)
    c: Coincident(g205,g202)
    c: Coincident(g205,g37)
    c: Coincident(g206,g37)
    c: Coincident(g206,g196)
    c: Coincident(g207,g196)
    c: Coincident(g207,g202)
    c: Vertical(g207)
    c: Weight(g208) = 1
    c: Equal(g208,g209)
    c: Equal(g208,g210)
    c: InternalAlignment(g208,g211)
    c: InternalAlignment(g209,g211)
    c: InternalAlignment(g210,g211)
    c: InternalAlignment(g212,g211)
    c: InternalAlignment(g213,g211)
    c: Weight(g214) = 1
    c: Equal(g214,g215)
    c: Equal(g214,g216)
    c: InternalAlignment(g214,g217)
    c: InternalAlignment(g215,g217)
    c: InternalAlignment(g216,g217)
    c: InternalAlignment(g218,g217)
    c: InternalAlignment(g219,g217)
    c: Block(g217)
    c: Block(g211)
    c: Coincident(g220,g211)
    c: Coincident(g220,g43)
    c: Coincident(g221,g43)
    c: Coincident(g221,g217)
    c: Coincident(g222,g217)
    c: Coincident(g222,g211)
    c: Vertical(g222)
    c: Horizontal(g223)
    c: Block(g223)
    c: Vertical(g224)
    c: Block(g224)
    c: Block(g225)
    c: Weight(g226) = 1
    c: Equal(g226,g227)
    c: Equal(g226,g228)
    c: InternalAlignment(g226,g229)
    c: InternalAlignment(g227,g229)
    c: InternalAlignment(g228,g229)
    c: InternalAlignment(g230,g229)
    c: InternalAlignment(g231,g229)
    c: Weight(g232) = 1
    c: Equal(g232,g233)
    c: Equal(g232,g234)
    c: InternalAlignment(g232,g235)
    c: InternalAlignment(g233,g235)
    c: InternalAlignment(g234,g235)
    c: InternalAlignment(g236,g235)
    c: InternalAlignment(g237,g235)
    c: Weight(g238) = 1
    c: Equal(g238,g239)
    c: Equal(g238,g240)
    c: InternalAlignment(g238,g241)
    c: InternalAlignment(g239,g241)
    c: InternalAlignment(g240,g241)
    c: InternalAlignment(g242,g241)
    c: InternalAlignment(g243,g241)
    c: Weight(g244) = 1
    c: Equal(g244,g245)
    c: Equal(g244,g246)
    c: InternalAlignment(g244,g247)
    c: InternalAlignment(g245,g247)
    c: InternalAlignment(g246,g247)
    c: InternalAlignment(g248,g247)
    c: InternalAlignment(g249,g247)
    c: Block(g229)
    c: Block(g235)
    c: Block(g241)
    c: Block(g247)
    c: Coincident(g250,g235)
    c: Coincident(g250,g229)
    c: Horizontal(g250)
    c: Block(g192)
    c: Weight(g251) = 1
    c: Equal(g251,g252)
    c: Equal(g251,g253)
    c: InternalAlignment(g251,g254)
    c: InternalAlignment(g252,g254)
    c: InternalAlignment(g253,g254)
    c: InternalAlignment(g255,g254)
    c: InternalAlignment(g256,g254)
    c: Weight(g257) = 1
    c: Equal(g257,g258)
    c: Equal(g257,g259)
    c: InternalAlignment(g257,g260)
    c: InternalAlignment(g258,g260)
    c: InternalAlignment(g259,g260)
    c: InternalAlignment(g261,g260)
    c: InternalAlignment(g262,g260)
    c: Block(g254)
    c: Block(g260)
    c: Coincident(g263,g254)
    c: Coincident(g263,g260)
    c: Weight(g264) = 1
    c: Equal(g264,g265)
    c: Equal(g264,g266)
    c: InternalAlignment(g264,g267)
    c: InternalAlignment(g265,g267)
    c: InternalAlignment(g266,g267)
    c: InternalAlignment(g268,g267)
    c: InternalAlignment(g269,g267)
    c: Weight(g270) = 1
    c: Equal(g270,g271)
    c: Equal(g270,g272)
    c: InternalAlignment(g270,g273)
    c: InternalAlignment(g271,g273)
    c: InternalAlignment(g272,g273)
    c: InternalAlignment(g274,g273)
    c: InternalAlignment(g275,g273)
    c: Weight(g276) = 1
    c: Equal(g276,g277)
    c: Equal(g276,g278)
    c: InternalAlignment(g276,g279)
    c: InternalAlignment(g277,g279)
    c: InternalAlignment(g278,g279)
    c: InternalAlignment(g280,g279)
    c: InternalAlignment(g281,g279)
    c: Block(g279)
    c: Block(g273)
    c: Block(g267)
    c: Coincident(g282,g273)
    c: Coincident(g282,g267)
    c: Coincident(g283,g267)
    c: Coincident(g283,g279)
    c: Vertical(g283)
    c: Coincident(g284,g279)
    c: Coincident(g284,g273)
    c: Horizontal(g284)
    c: Weight(g285) = 1
    c: Equal(g285,g286)
    c: InternalAlignment(g285,g287)
    c: InternalAlignment(g286,g287)
    c: InternalAlignment(g288,g287)
    c: InternalAlignment(g289,g287)
    c: Weight(g290) = 1
    c: InternalAlignment(g291,g293)
    c: InternalAlignment(g292,g293)
    c: InternalAlignment(g294,g293)
    c: InternalAlignment(g295,g293)
    c: Weight(g296) = 1
    c: Equal(g296,g297)
    c: Equal(g296,g298)
    c: InternalAlignment(g296,g299)
    c: InternalAlignment(g297,g299)
    c: InternalAlignment(g298,g299)
    c: InternalAlignment(g300,g299)
    c: InternalAlignment(g301,g299)
    c: Equal(g302,g303)
    c: Equal(g302,g304)
    c: InternalAlignment(g302,g305)
    c: InternalAlignment(g303,g305)
    c: InternalAlignment(g304,g305)
    c: InternalAlignment(g306,g305)
    c: InternalAlignment(g307,g305)
    c: Block(g293)
    c: Block(g299)
    c: Block(g305)
    c: Block(g287)
    c: Coincident(g308,g287)
    c: Coincident(g308,g293)
    c: Horizontal(g308)
    c: Coincident(g309,g293)
    c: Coincident(g309,g299)
    c: Vertical(g309)
    c: Coincident(g310,g299)
    c: Coincident(g310,g305)
    c: Horizontal(g310)
    c: Coincident(g311,g305)
    c: Coincident(g311,g287)
    c: Weight(g312) = 1
    c: Equal(g312,g313)
    c: Equal(g312,g314)
    c: InternalAlignment(g312,g315)
    c: InternalAlignment(g313,g315)
    c: InternalAlignment(g314,g315)
    c: InternalAlignment(g316,g315)
    c: InternalAlignment(g317,g315)
    c: Weight(g318) = 1
    c: Equal(g318,g319)
    c: Equal(g318,g320)
    c: InternalAlignment(g318,g321)
    c: InternalAlignment(g319,g321)
    c: InternalAlignment(g320,g321)
    c: InternalAlignment(g322,g321)
    c: InternalAlignment(g323,g321)
    c: Weight(g324) = 1
    c: Equal(g324,g325)
    c: Equal(g324,g326)
    c: InternalAlignment(g324,g327)
    c: InternalAlignment(g325,g327)
    c: InternalAlignment(g326,g327)
    c: InternalAlignment(g328,g327)
    c: InternalAlignment(g329,g327)
    c: Block(g327)
    c: Block(g321)
    c: Block(g315)
    c: Coincident(g330,g327)
    c: Coincident(g330,g321)
    c: Horizontal(g330)
    c: Coincident(g331,g321)
    c: Coincident(g331,g315)
    c: Vertical(g331)
    c: Coincident(g332,g315)
    c: Coincident(g332,g327)
    c: InternalAlignment(g333,g334)
    c: InternalAlignment(g335,g334)
    c: InternalAlignment(g336,g334)
    c: Block(g334)
    c: Equal(g337,g338)
    c: Equal(g337,g339)
    c: InternalAlignment(g337,g340)
    c: InternalAlignment(g338,g340)
    c: InternalAlignment(g339,g340)
    c: InternalAlignment(g341,g340)
    c: InternalAlignment(g342,g340)
    c: Block(g340)
    c: Coincident(g343,g334)
    c: Horizontal(g343)
    c: Block(g343)
    c: Coincident(g344,g334)
    c: Coincident(g344,g260)
    c: Vertical(g344)
    c: Coincident(g345,g340)
    c: Coincident(g345,g254)
    c: Vertical(g345)
    c: Coincident(g347,g5)
    c: Coincident(g348,g5)
    c: Block(g346)
    c: Block(g5)
    c: Block(g348)
    c: Block(g347)
    c: Distance(g344) = 119.89
FEATURE [Sketcher::SketchObject] Sketch001
  FullyConstrained = true
  MapMode = 4
  Placement = pos=(0,0,0) rot=(0.57735,0.57735,0.57735;2.0944rad)
  Support = -> [Sketch]
  sketch-geometry (46):
    g0: BSplineCurve PolesCount=3 KnotsCount=2 Degree=2 IsPeriodic=0
    g1: ArcOfCircle CenterX=73.1223 CenterY=-32.291 CenterZ=0 NormalX=0 NormalY=0 NormalZ=1 AngleXU=0 Radius=13 StartAngle=5.92268 EndAngle=9.06428
    g2: ArcOfCircle CenterX=66.7816 CenterY=-49.1439 CenterZ=0 NormalX=0 NormalY=0 NormalZ=1 AngleXU=0 Radius=13 StartAngle=2.78068 EndAngle=5.92131
    g3: ArcOfCircle CenterX=55.9263 CenterY=-78.1807 CenterZ=0 NormalX=0 NormalY=0 NormalZ=1 AngleXU=0 Radius=13 StartAngle=5.92268 EndAngle=9.06428
    g4: ArcOfCircle CenterX=49.5884 CenterY=-95.0342 CenterZ=0 NormalX=0 NormalY=0 NormalZ=1 AngleXU=0 Radius=13 StartAngle=2.78068 EndAngle=5.92131
    g5: ArcOfCircle CenterX=38.7206 CenterY=-124.067 CenterZ=0 NormalX=0 NormalY=0 NormalZ=1 AngleXU=0 Radius=13 StartAngle=5.92268 EndAngle=9.06428
    g6: ArcOfCircle CenterX=32.3875 CenterY=-140.92 CenterZ=0 NormalX=0 NormalY=0 NormalZ=1 AngleXU=0 Radius=13 StartAngle=2.78068 EndAngle=5.92131
    g7: ArcOfCircle CenterX=21.4715 CenterY=-169.934 CenterZ=0 NormalX=0 NormalY=0 NormalZ=1 AngleXU=0 Radius=13 StartAngle=5.92268 EndAngle=9.06428
    g8: ArcOfCircle CenterX=15.1336 CenterY=-186.787 CenterZ=0 NormalX=0 NormalY=0 NormalZ=1 AngleXU=0 Radius=13 StartAngle=2.78068 EndAngle=5.92131
    g9-g12: Circle x4 (B-spline internal-alignment scaffolding for g13; pole/knot coordinates omitted)
    g13: BSplineCurve PolesCount=4 KnotsCount=2 Degree=3 IsPeriodic=0
    g14: GeomPoint X=28.8094 Y=-19.0875 Z=0
    g15: GeomPoint X=47.0443 Y=-50.4712 Z=0
    g16: Circle CenterX=53.5586 CenterY=-23.2695 CenterZ=0 NormalX=0 NormalY=0 NormalZ=1 AngleXU=0 Radius=3.24518
    g17: Circle CenterX=-195.441 CenterY=-127.082 CenterZ=0 NormalX=0 NormalY=0 NormalZ=1 AngleXU=0 Radius=1
    g18: Circle CenterX=-8.24091 CenterY=-197.481 CenterZ=0 NormalX=0 NormalY=0 NormalZ=1 AngleXU=0 Radius=1
    g19: Circle CenterX=12.8789 CenterY=-141.321 CenterZ=0 NormalX=0 NormalY=0 NormalZ=1 AngleXU=0 Radius=1
    g20: BSplineCurve PolesCount=3 KnotsCount=2 Degree=2 IsPeriodic=0
    g21: GeomPoint X=-195.441 Y=-127.082 Z=0
    g22: GeomPoint X=12.8789 Y=-141.321 Z=0
    g23: Circle CenterX=-12.8016 CenterY=-179.036 CenterZ=0 NormalX=0 NormalY=0 NormalZ=1 AngleXU=0 Radius=10.5072
    g24: Circle CenterX=0.933922 CenterY=-166.43 CenterZ=0 NormalX=0 NormalY=0 NormalZ=1 AngleXU=0 Radius=3.26661
    g25: Circle CenterX=-33.5518 CenterY=-176.44 CenterZ=0 NormalX=0 NormalY=0 NormalZ=1 AngleXU=0 Radius=5.64388
    g26: Circle CenterX=-47.2366 CenterY=-173.859 CenterZ=0 NormalX=0 NormalY=0 NormalZ=1 AngleXU=0 Radius=3.01653
    g27: Circle CenterX=-56.2595 CenterY=-171.456 CenterZ=0 NormalX=0 NormalY=0 NormalZ=1 AngleXU=0 Radius=2.12826
    g28: ArcOfCircle CenterX=51.2151 CenterY=-198.473 CenterZ=0 NormalX=0 NormalY=0 NormalZ=1 AngleXU=0 Radius=20 StartAngle=2.78189 EndAngle=4.35269
    g29: LineSegment StartX=32.4951 StartY=-191.433 StartZ=0 EndX=94.6578 EndY=-26.1352 EndZ=0
    g30: LineSegment StartX=43.1192 StartY=-220.001 StartZ=0 EndX=-196.497 EndY=-129.89 EndZ=0
    g31: LineSegment StartX=43.1192 StartY=-220.001 StartZ=0 EndX=44.1752 EndY=-217.193 EndZ=0
    g32: LineSegment StartX=117.223 StartY=-19.0875 StartZ=0 EndX=117.223 EndY=-16.0875 EndZ=0
    g33: LineSegment StartX=117.223 StartY=-16.0875 StartZ=0 EndX=17.2232 EndY=-16.0875 EndZ=0
    g34: LineSegment StartX=17.2232 StartY=-16.0875 StartZ=0 EndX=17.2232 EndY=-19.0875 EndZ=0
    g35: LineSegment StartX=28.8094 StartY=-19.0875 StartZ=0 EndX=17.2232 EndY=-19.0875 EndZ=0
    g36: LineSegment StartX=47.0443 StartY=-50.4712 StartZ=0 EndX=12.8789 EndY=-141.321 EndZ=0
    g37: LineSegment StartX=-195.441 StartY=-127.082 StartZ=0 EndX=-196.497 EndY=-129.89 EndZ=0
    g38: LineSegment StartX=85.2866 StartY=-36.8766 StartZ=0 EndX=78.9396 EndY=-53.7463 EndZ=0
    g39: LineSegment StartX=60.9579 StartY=-27.7053 StartZ=0 EndX=54.6191 EndY=-44.5532 EndZ=0
    g40: LineSegment StartX=68.0907 StartY=-82.7664 StartZ=0 EndX=61.7465 EndY=-99.6365 EndZ=0
    g41: LineSegment StartX=43.7619 StartY=-73.595 StartZ=0 EndX=37.426 EndY=-90.4435 EndZ=0
    g42: LineSegment StartX=50.885 StartY=-128.652 StartZ=0 EndX=44.5456 EndY=-145.522 EndZ=0
    g43: LineSegment StartX=26.5562 StartY=-119.481 StartZ=0 EndX=20.2251 EndY=-136.329 EndZ=0
    g44: LineSegment StartX=9.3071 StartY=-165.349 StartZ=0 EndX=2.97115 EndY=-182.197 EndZ=0
    g45: LineSegment StartX=33.6358 StartY=-174.52 StartZ=0 EndX=27.2917 EndY=-191.39 EndZ=0
  constraints (71):
    c: Block(g0)
    c: Block(g1)
    c: Block(g2)
    c: Block(g4)
    c: Block(g3)
    c: Block(g6)
    c: Block(g5)
    c: Block(g8)
    c: Block(g7)
    c: Weight(g9) = 1
    c: Equal(g9,g10)
    c: Equal(g9,g11)
    c: Equal(g9,g12)
    c: InternalAlignment(g9-g12 -> g13) x4
    c: InternalAlignment(g14,g13)
    c: InternalAlignment(g15,g13)
    c: Block(g16)
    c: Weight(g17) = 1
    c: Equal(g17,g18)
    c: Equal(g17,g19)
    c: InternalAlignment(g17,g20)
    c: InternalAlignment(g18,g20)
    c: InternalAlignment(g19,g20)
    c: InternalAlignment(g21,g20)
    c: InternalAlignment(g22,g20)
    c: Block(g20)
    c: Block(g23)
    c: Block(g24)
    c: Block(g25)
    c: Block(g26)
    c: Block(g27)
    c: Block(g28)
    c: Coincident(g29,g28)
    c: Coincident(g29,g0)
    c: Block(g13)
    c: Coincident(g31,g30)
    c: Coincident(g31,g28)
    c: Block(g31)
    c: Coincident(g32,g0)
    c: Vertical(g32)
    c: Coincident(g33,g32)
    c: Horizontal(g33)
    c: Coincident(g34,g33)
    c: Vertical(g34)
    c: Block(g33)
    c: Coincident(g35,g13)
    c: Coincident(g35,g34)
    c: Horizontal(g35)
    c: Coincident(g36,g13)
    c: Coincident(g36,g20)
    c: Coincident(g37,g20)
    c: Coincident(g37,g30)
    c: Block(g30)
    c: Coincident(g38,g1)
    c: Coincident(g38,g2)
    c: Coincident(g39,g1)
    c: Coincident(g39,g2)
    c: Coincident(g40,g3)
    c: Coincident(g40,g4)
    c: Coincident(g41,g3)
    c: Coincident(g41,g4)
    c: Coincident(g42,g5)
    c: Coincident(g42,g6)
    c: Coincident(g43,g5)
    c: Coincident(g43,g6)
    c: Coincident(g44,g7)
    c: Coincident(g44,g8)
    c: Coincident(g45,g7)
    c: Coincident(g45,g8)
    c: Distance(g30) = 256
    c: Distance(g33) = 100
FEATURE [Part::Extrusion] Extrude002
  Base = -> Sketch001
  Dir = (1,0,0)
  DirMode = 2
  FaceMakerClass = Part::FaceMakerBullseye
  LengthFwd = 8
  LengthRev = 0
  Solid = true
  Symmetric = false
FEATURE [Sketcher::SketchObject] Sketch002
  FullyConstrained = true
  sketch-geometry (20):
    g0: LineSegment StartX=-2.77179 StartY=-200.304 StartZ=0 EndX=5.22821 EndY=-200.304 EndZ=0
    g1: LineSegment StartX=5.22821 StartY=-200.304 StartZ=0 EndX=5.22821 EndY=-197.304 EndZ=0
    g2: LineSegment StartX=-2.77179 StartY=-200.304 StartZ=0 EndX=-2.77179 EndY=-197.304 EndZ=0
    g3: LineSegment StartX=5.22821 StartY=-197.304 StartZ=0 EndX=8.22821 EndY=-197.304 EndZ=0
    g4: LineSegment StartX=-2.77179 StartY=-197.304 StartZ=0 EndX=-5.77179 EndY=-197.304 EndZ=0
    g5: LineSegment StartX=19.2282 StartY=-203.304 StartZ=0 EndX=19.2282 EndY=-206.304 EndZ=0
    g6: LineSegment StartX=-16.7718 StartY=-203.304 StartZ=0 EndX=-16.7718 EndY=-206.304 EndZ=0
    g7: LineSegment StartX=-16.7718 StartY=-206.304 StartZ=0 EndX=19.2282 EndY=-206.304 EndZ=0
    g8: Circle CenterX=-16.7718 CenterY=-203.304 CenterZ=0 NormalX=0 NormalY=0 NormalZ=1 AngleXU=0 Radius=1
    g9: Circle CenterX=-5.77179 CenterY=-203.304 CenterZ=0 NormalX=0 NormalY=0 NormalZ=1 AngleXU=0 Radius=1
    g10: Circle CenterX=-5.77179 CenterY=-197.304 CenterZ=0 NormalX=0 NormalY=0 NormalZ=1 AngleXU=0 Radius=1
    g11: BSplineCurve PolesCount=3 KnotsCount=2 Degree=2 IsPeriodic=0
    g12: GeomPoint X=-16.7718 Y=-203.304 Z=0
    g13: GeomPoint X=-5.77179 Y=-197.304 Z=0
    g14: Circle CenterX=19.2282 CenterY=-203.304 CenterZ=0 NormalX=0 NormalY=0 NormalZ=1 AngleXU=0 Radius=1
    g15: Circle CenterX=8.22821 CenterY=-203.304 CenterZ=0 NormalX=0 NormalY=0 NormalZ=1 AngleXU=0 Radius=1
    g16: Circle CenterX=8.22821 CenterY=-197.304 CenterZ=0 NormalX=0 NormalY=0 NormalZ=1 AngleXU=0 Radius=1
    g17: BSplineCurve PolesCount=3 KnotsCount=2 Degree=2 IsPeriodic=0
    g18: GeomPoint X=19.2282 Y=-203.304 Z=0
    g19: GeomPoint X=8.22821 Y=-197.304 Z=0
  constraints (41):
    c: Horizontal(g0)
    c: Distance(g0) = 8
    c: Coincident(g1,g0)
    c: Vertical(g1)
    c: Distance(g1) = 3
    c: Coincident(g2,g0)
    c: Vertical(g2)
    c: Distance(g2) = 3
    c: Coincident(g3,g1)
    c: Horizontal(g3)
    c: Distance(g3) = 3
    c: Coincident(g4,g2)
    c: Horizontal(g4)
    c: Distance(g4) = 3
    c: Vertical(g5)
    c: Vertical(g6)
    c: Coincident(g7,g6)
    c: Coincident(g7,g5)
    c: Weight(g8) = 1
    c: Equal(g8,g9)
    c: Equal(g8,g10)
    c: Coincident(g11,g4)
    c: InternalAlignment(g8,g11)
    c: InternalAlignment(g9,g11)
    c: InternalAlignment(g10,g11)
    c: InternalAlignment(g12,g11)
    c: InternalAlignment(g13,g11)
    c: Coincident(g17,g5)
    c: Weight(g14) = 1
    c: Equal(g14,g15)
    c: Equal(g14,g16)
    c: Coincident(g17,g3)
    c: InternalAlignment(g14,g17)
    c: InternalAlignment(g15,g17)
    c: InternalAlignment(g16,g17)
    c: InternalAlignment(g18,g17)
    c: InternalAlignment(g19,g17)
    c: Block(g7)
    c: Block(g17)
    c: Block(g11)
    c: Block(g6)
FEATURE [Part::Extrusion] Extrude003
  Base = -> Sketch002
  Dir = (0,0,1)
  DirMode = 2
  FaceMakerClass = Part::FaceMakerBullseye
  LengthFwd = 260
  LengthRev = 0
  Solid = true
  Symmetric = false
FEATURE [Sketcher::SketchObject] Sketch003
  FullyConstrained = false
  sketch-geometry (377):
    g0: LineSegment StartX=-42.9272 StartY=136.221 StartZ=0 EndX=-42.9272 EndY=-103.779 EndZ=0
    g1: LineSegment StartX=407.073 StartY=136.221 StartZ=0 EndX=407.073 EndY=-103.779 EndZ=0
    g2: ArcOfCircle CenterX=-26.9272 CenterY=-83.7794 CenterZ=0 NormalX=0 NormalY=0 NormalZ=1 AngleXU=0 Radius=8 StartAngle=3.14159 EndAngle=6.28319
    g3: ArcOfCircle CenterX=391.073 CenterY=-83.7794 CenterZ=0 NormalX=0 NormalY=0 NormalZ=1 AngleXU=0 Radius=8 StartAngle=3.14159 EndAngle=6.28319
    g4: Circle CenterX=175.022 CenterY=27.0628 CenterZ=0 NormalX=0 NormalY=0 NormalZ=1 AngleXU=0 Radius=1
    g5: Circle CenterX=179.022 CenterY=24.8665 CenterZ=0 NormalX=0 NormalY=0 NormalZ=1 AngleXU=0 Radius=1
    g6: Circle CenterX=179.022 CenterY=27.0628 CenterZ=0 NormalX=0 NormalY=0 NormalZ=1 AngleXU=0 Radius=1
    g7: BSplineCurve PolesCount=3 KnotsCount=2 Degree=2 IsPeriodic=0
    g8: GeomPoint X=175.022 Y=27.0628 Z=0
    g9: GeomPoint X=179.022 Y=27.0628 Z=0
    g10: Circle CenterX=189.124 CenterY=27.0628 CenterZ=0 NormalX=0 NormalY=0 NormalZ=1 AngleXU=0 Radius=1
    g11: Circle CenterX=185.124 CenterY=24.8665 CenterZ=0 NormalX=0 NormalY=0 NormalZ=1 AngleXU=0 Radius=1
    g12: Circle CenterX=185.124 CenterY=27.0628 CenterZ=0 NormalX=0 NormalY=0 NormalZ=1 AngleXU=0 Radius=1
    g13: BSplineCurve PolesCount=3 KnotsCount=2 Degree=2 IsPeriodic=0
    g14: GeomPoint X=189.124 Y=27.0628 Z=0
    g15: GeomPoint X=185.124 Y=27.0628 Z=0
    g16: Circle CenterX=175.022 CenterY=5.37834 CenterZ=0 NormalX=0 NormalY=0 NormalZ=1 AngleXU=0 Radius=1
    g17: Circle CenterX=179.022 CenterY=7.57463 CenterZ=0 NormalX=0 NormalY=0 NormalZ=1 AngleXU=0 Radius=1
    g18: Circle CenterX=179.022 CenterY=5.34704 CenterZ=0 NormalX=0 NormalY=0 NormalZ=1 AngleXU=0 Radius=1
    g19: BSplineCurve PolesCount=3 KnotsCount=2 Degree=2 IsPeriodic=0
    g20: GeomPoint X=175.022 Y=5.37834 Z=0
    g21: GeomPoint X=179.022 Y=5.34704 Z=0
    g22: Circle CenterX=189.124 CenterY=5.37834 CenterZ=0 NormalX=0 NormalY=0 NormalZ=1 AngleXU=0 Radius=1
    g23: Circle CenterX=185.124 CenterY=7.57463 CenterZ=0 NormalX=0 NormalY=0 NormalZ=1 AngleXU=0 Radius=1
    g24: Circle CenterX=185.124 CenterY=5.34704 CenterZ=0 NormalX=0 NormalY=0 NormalZ=1 AngleXU=0 Radius=1
    g25: BSplineCurve PolesCount=3 KnotsCount=2 Degree=2 IsPeriodic=0
    g26: GeomPoint X=189.124 Y=5.37834 Z=0
    g27: GeomPoint X=185.124 Y=5.34704 Z=0
    g28: Circle CenterX=165.871 CenterY=18.1458 CenterZ=0 NormalX=0 NormalY=0 NormalZ=1 AngleXU=0 Radius=1
    g29: Circle CenterX=169.377 CenterY=16.2206 CenterZ=0 NormalX=0 NormalY=0 NormalZ=1 AngleXU=0 Radius=1
    g30: Circle CenterX=165.871 CenterY=14.2954 CenterZ=0 NormalX=0 NormalY=0 NormalZ=1 AngleXU=0 Radius=1
    g31: BSplineCurve PolesCount=3 KnotsCount=2 Degree=2 IsPeriodic=0
    g32: GeomPoint X=165.871 Y=18.1458 Z=0
    g33: GeomPoint X=165.871 Y=14.2954 Z=0
    g34: Circle CenterX=198.275 CenterY=18.1458 CenterZ=0 NormalX=0 NormalY=0 NormalZ=1 AngleXU=0 Radius=1
    g35: Circle CenterX=194.768 CenterY=16.2206 CenterZ=0 NormalX=0 NormalY=0 NormalZ=1 AngleXU=0 Radius=1
    g36: Circle CenterX=198.275 CenterY=14.2954 CenterZ=0 NormalX=0 NormalY=0 NormalZ=1 AngleXU=0 Radius=1
    g37: BSplineCurve PolesCount=3 KnotsCount=2 Degree=2 IsPeriodic=0
    g38: GeomPoint X=198.275 Y=18.1458 Z=0
    g39: GeomPoint X=198.275 Y=14.2954 Z=0
    g40: LineSegment StartX=407.073 StartY=-103.779 StartZ=0 EndX=-42.9272 EndY=-103.779 EndZ=0
    g41: Circle CenterX=125.607 CenterY=54.1951 CenterZ=0 NormalX=0 NormalY=0 NormalZ=1 AngleXU=0 Radius=1
    g42: Circle CenterX=139.632 CenterY=46.4944 CenterZ=0 NormalX=0 NormalY=0 NormalZ=1 AngleXU=0 Radius=1
    g43: Circle CenterX=127.326 CenterY=56.7187 CenterZ=0 NormalX=0 NormalY=0 NormalZ=1 AngleXU=0 Radius=1
    g44: BSplineCurve PolesCount=3 KnotsCount=2 Degree=2 IsPeriodic=0
    g45: GeomPoint X=125.607 Y=54.1951 Z=0
    g46: GeomPoint X=127.326 Y=56.7187 Z=0
    g47: Circle CenterX=236.821 CenterY=56.7187 CenterZ=0 NormalX=0 NormalY=0 NormalZ=1 AngleXU=0 Radius=1
    g48: Circle CenterX=224.513 CenterY=46.4944 CenterZ=0 NormalX=0 NormalY=0 NormalZ=1 AngleXU=0 Radius=1
    g49: Circle CenterX=238.538 CenterY=54.1951 CenterZ=0 NormalX=0 NormalY=0 NormalZ=1 AngleXU=0 Radius=1
    g50: BSplineCurve PolesCount=3 KnotsCount=2 Degree=2 IsPeriodic=0
    g51: GeomPoint X=236.821 Y=56.7187 Z=0
    g52: GeomPoint X=238.538 Y=54.1951 Z=0
    g53: Circle CenterX=238.538 CenterY=-21.7539 CenterZ=0 NormalX=0 NormalY=0 NormalZ=1 AngleXU=0 Radius=1
    g54: Circle CenterX=224.513 CenterY=-14.0532 CenterZ=0 NormalX=0 NormalY=0 NormalZ=1 AngleXU=0 Radius=1
    g55: Circle CenterX=236.821 CenterY=-24.2775 CenterZ=0 NormalX=0 NormalY=0 NormalZ=1 AngleXU=0 Radius=1
    g56: BSplineCurve PolesCount=3 KnotsCount=2 Degree=2 IsPeriodic=0
    g57: GeomPoint X=238.538 Y=-21.7539 Z=0
    g58: GeomPoint X=236.821 Y=-24.2775 Z=0
    g59: Circle CenterX=125.607 CenterY=-21.7539 CenterZ=0 NormalX=0 NormalY=0 NormalZ=1 AngleXU=0 Radius=1
    g60: Circle CenterX=139.632 CenterY=-14.0532 CenterZ=0 NormalX=0 NormalY=0 NormalZ=1 AngleXU=0 Radius=1
    g61: Circle CenterX=127.325 CenterY=-24.2775 CenterZ=0 NormalX=0 NormalY=0 NormalZ=1 AngleXU=0 Radius=1
    g62: BSplineCurve PolesCount=3 KnotsCount=2 Degree=2 IsPeriodic=0
    g63: GeomPoint X=125.607 Y=-21.7539 Z=0
    g64: GeomPoint X=127.325 Y=-24.2775 Z=0
    g65: Circle CenterX=302.996 CenterY=111.695 CenterZ=0 NormalX=0 NormalY=0 NormalZ=1 AngleXU=0 Radius=1
    g66: Circle CenterX=306.073 CenterY=114.251 CenterZ=0 NormalX=0 NormalY=0 NormalZ=1 AngleXU=0 Radius=1
    g67: Circle CenterX=306.073 CenterY=110.251 CenterZ=0 NormalX=0 NormalY=0 NormalZ=1 AngleXU=0 Radius=1
    g68: BSplineCurve PolesCount=3 KnotsCount=2 Degree=2 IsPeriodic=0
    g69: GeomPoint X=302.996 Y=111.695 Z=0
    g70: GeomPoint X=306.073 Y=110.251 Z=0
    g71: Circle CenterX=306.073 CenterY=95.2763 CenterZ=0 NormalX=0 NormalY=0 NormalZ=1 AngleXU=0 Radius=1
    g72: Circle CenterX=306.073 CenterY=91.2763 CenterZ=0 NormalX=0 NormalY=0 NormalZ=1 AngleXU=0 Radius=1
    g73: Circle CenterX=302.567 CenterY=89.3511 CenterZ=0 NormalX=0 NormalY=0 NormalZ=1 AngleXU=0 Radius=1
    g74: BSplineCurve PolesCount=3 KnotsCount=2 Degree=2 IsPeriodic=0
    g75: GeomPoint X=306.073 Y=95.2763 Z=0
    g76: GeomPoint X=302.567 Y=89.3511 Z=0
    g77: LineSegment StartX=306.073 StartY=110.251 StartZ=0 EndX=306.073 EndY=95.2763 EndZ=0
    g78: LineSegment StartX=302.996 StartY=111.695 StartZ=0 EndX=236.821 EndY=56.7187 EndZ=0
    g79: LineSegment StartX=238.538 StartY=54.1951 StartZ=0 EndX=302.567 EndY=89.3511 EndZ=0
    g80: Circle CenterX=61.1496 CenterY=111.695 CenterZ=0 NormalX=0 NormalY=0 NormalZ=1 AngleXU=0 Radius=1
    g81: Circle CenterX=58.0728 CenterY=114.251 CenterZ=0 NormalX=0 NormalY=0 NormalZ=1 AngleXU=0 Radius=1
    g82: Circle CenterX=58.0728 CenterY=110.251 CenterZ=0 NormalX=0 NormalY=0 NormalZ=1 AngleXU=0 Radius=1
    g83: BSplineCurve PolesCount=3 KnotsCount=2 Degree=2 IsPeriodic=0
    g84: GeomPoint X=61.1496 Y=111.695 Z=0
    g85: GeomPoint X=58.0728 Y=110.251 Z=0
    g86: Circle CenterX=61.5791 CenterY=89.3511 CenterZ=0 NormalX=0 NormalY=0 NormalZ=1 AngleXU=0 Radius=1
    g87: Circle CenterX=58.0728 CenterY=91.2763 CenterZ=0 NormalX=0 NormalY=0 NormalZ=1 AngleXU=0 Radius=1
    g88: Circle CenterX=58.0728 CenterY=95.2763 CenterZ=0 NormalX=0 NormalY=0 NormalZ=1 AngleXU=0 Radius=1
    g89: BSplineCurve PolesCount=3 KnotsCount=2 Degree=2 IsPeriodic=0
    g90: GeomPoint X=61.5791 Y=89.3511 Z=0
    g91: GeomPoint X=58.0728 Y=95.2763 Z=0
    g92: LineSegment StartX=58.0728 StartY=110.251 StartZ=0 EndX=58.0728 EndY=95.2763 EndZ=0
    g93: LineSegment StartX=61.1496 StartY=111.695 StartZ=0 EndX=127.326 EndY=56.7187 EndZ=0
    g94: LineSegment StartX=125.607 StartY=54.1951 StartZ=0 EndX=61.5791 EndY=89.3511 EndZ=0
    g95: Circle CenterX=61.5791 CenterY=-56.9099 CenterZ=0 NormalX=0 NormalY=0 NormalZ=1 AngleXU=0 Radius=1
    g96: Circle CenterX=58.0728 CenterY=-58.8351 CenterZ=0 NormalX=0 NormalY=0 NormalZ=1 AngleXU=0 Radius=1
    g97: Circle CenterX=58.0728 CenterY=-62.8351 CenterZ=0 NormalX=0 NormalY=0 NormalZ=1 AngleXU=0 Radius=1
    g98: BSplineCurve PolesCount=3 KnotsCount=2 Degree=2 IsPeriodic=0
    g99: GeomPoint X=61.5791 Y=-56.9099 Z=0
    g100: GeomPoint X=58.0728 Y=-62.8351 Z=0
    g101: Circle CenterX=58.0728 CenterY=-77.8102 CenterZ=0 NormalX=0 NormalY=0 NormalZ=1 AngleXU=0 Radius=1
    g102: Circle CenterX=58.0728 CenterY=-81.8102 CenterZ=0 NormalX=0 NormalY=0 NormalZ=1 AngleXU=0 Radius=1
    g103: Circle CenterX=61.1496 CenterY=-79.2541 CenterZ=0 NormalX=0 NormalY=0 NormalZ=1 AngleXU=0 Radius=1
    g104: BSplineCurve PolesCount=3 KnotsCount=2 Degree=2 IsPeriodic=0
    g105: GeomPoint X=58.0728 Y=-77.8102 Z=0
    g106: GeomPoint X=61.1496 Y=-79.2541 Z=0
    g107: LineSegment StartX=58.0728 StartY=-62.8351 StartZ=0 EndX=58.0728 EndY=-77.8102 EndZ=0
    g108: LineSegment StartX=61.1496 StartY=-79.2541 StartZ=0 EndX=127.325 EndY=-24.2775 EndZ=0
    g109: LineSegment StartX=125.607 StartY=-21.7539 StartZ=0 EndX=61.5791 EndY=-56.9099 EndZ=0
    g110: Circle CenterX=302.567 CenterY=-56.9099 CenterZ=0 NormalX=0 NormalY=0 NormalZ=1 AngleXU=0 Radius=1
    g111: Circle CenterX=306.073 CenterY=-58.8351 CenterZ=0 NormalX=0 NormalY=0 NormalZ=1 AngleXU=0 Radius=1
    g112: Circle CenterX=306.073 CenterY=-62.8351 CenterZ=0 NormalX=0 NormalY=0 NormalZ=1 AngleXU=0 Radius=1
    g113: BSplineCurve PolesCount=3 KnotsCount=2 Degree=2 IsPeriodic=0
    g114: GeomPoint X=302.567 Y=-56.9099 Z=0
    g115: GeomPoint X=306.073 Y=-62.8351 Z=0
    g116: Circle CenterX=302.996 CenterY=-79.2541 CenterZ=0 NormalX=0 NormalY=0 NormalZ=1 AngleXU=0 Radius=1
    g117: Circle CenterX=306.073 CenterY=-81.8102 CenterZ=0 NormalX=0 NormalY=0 NormalZ=1 AngleXU=0 Radius=1
    g118: Circle CenterX=306.073 CenterY=-77.8102 CenterZ=0 NormalX=0 NormalY=0 NormalZ=1 AngleXU=0 Radius=1
    g119: BSplineCurve PolesCount=3 KnotsCount=2 Degree=2 IsPeriodic=0
    g120: GeomPoint X=302.996 Y=-79.2541 Z=0
    g121: GeomPoint X=306.073 Y=-77.8102 Z=0
    g122: LineSegment StartX=306.073 StartY=-62.8351 StartZ=0 EndX=306.073 EndY=-77.8102 EndZ=0
    g123: LineSegment StartX=302.996 StartY=-79.2541 StartZ=0 EndX=236.821 EndY=-24.2775 EndZ=0
    g124: LineSegment StartX=238.538 StartY=-21.7539 StartZ=0 EndX=302.567 EndY=-56.9099 EndZ=0
    g125: Circle CenterX=61.6457 CenterY=-88.8112 CenterZ=0 NormalX=0 NormalY=0 NormalZ=1 AngleXU=0 Radius=1
    g126: Circle CenterX=58.0728 CenterY=-91.7794 CenterZ=0 NormalX=0 NormalY=0 NormalZ=1 AngleXU=0 Radius=1
    g127: Circle CenterX=63.9135 CenterY=-91.7794 CenterZ=0 NormalX=0 NormalY=0 NormalZ=1 AngleXU=0 Radius=1
    g128: BSplineCurve PolesCount=3 KnotsCount=2 Degree=2 IsPeriodic=0
    g129: GeomPoint X=61.6457 Y=-88.8112 Z=0
    g130: GeomPoint X=63.9135 Y=-91.7794 Z=0
    g131: Circle CenterX=179.022 CenterY=-85.8163 CenterZ=0 NormalX=0 NormalY=0 NormalZ=1 AngleXU=0 Radius=1
    g132: Circle CenterX=179.022 CenterY=-91.7794 CenterZ=0 NormalX=0 NormalY=0 NormalZ=1 AngleXU=0 Radius=1
    g133: Circle CenterX=171.895 CenterY=-91.7794 CenterZ=0 NormalX=0 NormalY=0 NormalZ=1 AngleXU=0 Radius=1
    g134: BSplineCurve PolesCount=3 KnotsCount=2 Degree=2 IsPeriodic=0
    g135: GeomPoint X=179.022 Y=-85.8163 Z=0
    g136: GeomPoint X=171.895 Y=-91.7794 Z=0
    g137: Circle CenterX=185.124 CenterY=-86.2028 CenterZ=0 NormalX=0 NormalY=0 NormalZ=1 AngleXU=0 Radius=1
    g138: Circle CenterX=185.124 CenterY=-91.7794 CenterZ=0 NormalX=0 NormalY=0 NormalZ=1 AngleXU=0 Radius=1
    g139: Circle CenterX=191.747 CenterY=-91.7794 CenterZ=0 NormalX=0 NormalY=0 NormalZ=1 AngleXU=0 Radius=1
    g140: BSplineCurve PolesCount=3 KnotsCount=2 Degree=2 IsPeriodic=0
    g141: GeomPoint X=185.124 Y=-86.2028 Z=0
    g142: GeomPoint X=191.747 Y=-91.7794 Z=0
    g143: Circle CenterX=299.888 CenterY=-86.6413 CenterZ=0 NormalX=0 NormalY=0 NormalZ=1 AngleXU=0 Radius=1
    g144: Circle CenterX=306.073 CenterY=-91.7794 CenterZ=0 NormalX=0 NormalY=0 NormalZ=1 AngleXU=0 Radius=1
    g145: Circle CenterX=298.776 CenterY=-91.7794 CenterZ=0 NormalX=0 NormalY=0 NormalZ=1 AngleXU=0 Radius=1
    g146: BSplineCurve PolesCount=3 KnotsCount=2 Degree=2 IsPeriodic=0
    g147: GeomPoint X=299.888 Y=-86.6413 Z=0
    g148: GeomPoint X=298.776 Y=-91.7794 Z=0
    g149: LineSegment StartX=189.124 StartY=5.37834 StartZ=0 EndX=299.888 EndY=-86.6413 EndZ=0
    g150: LineSegment StartX=298.776 StartY=-91.7794 StartZ=0 EndX=191.747 EndY=-91.7794 EndZ=0
    g151: LineSegment StartX=185.124 StartY=-86.2028 StartZ=0 EndX=185.124 EndY=5.34704 EndZ=0
    g152: LineSegment StartX=179.022 StartY=5.34704 StartZ=0 EndX=179.022 EndY=-85.8163 EndZ=0
    g153: LineSegment StartX=171.895 StartY=-91.7794 StartZ=0 EndX=63.9135 EndY=-91.7794 EndZ=0
    g154: LineSegment StartX=61.6457 StartY=-88.8112 StartZ=0 EndX=175.022 EndY=5.37834 EndZ=0
    g155: Circle CenterX=302.073 CenterY=124.221 CenterZ=0 NormalX=0 NormalY=0 NormalZ=1 AngleXU=0 Radius=1
    g156: Circle CenterX=306.073 CenterY=124.221 CenterZ=0 NormalX=0 NormalY=0 NormalZ=1 AngleXU=0 Radius=1
    g157: Circle CenterX=302.996 CenterY=121.665 CenterZ=0 NormalX=0 NormalY=0 NormalZ=1 AngleXU=0 Radius=1
    g158: BSplineCurve PolesCount=3 KnotsCount=2 Degree=2 IsPeriodic=0
    g159: GeomPoint X=302.073 Y=124.221 Z=0
    g160: GeomPoint X=302.996 Y=121.665 Z=0
    g161: Circle CenterX=189.124 CenterY=124.221 CenterZ=0 NormalX=0 NormalY=0 NormalZ=1 AngleXU=0 Radius=1
    g162: Circle CenterX=185.124 CenterY=124.221 CenterZ=0 NormalX=0 NormalY=0 NormalZ=1 AngleXU=0 Radius=1
    g163: Circle CenterX=185.124 CenterY=120.221 CenterZ=0 NormalX=0 NormalY=0 NormalZ=1 AngleXU=0 Radius=1
    g164: BSplineCurve PolesCount=3 KnotsCount=2 Degree=2 IsPeriodic=0
    g165: GeomPoint X=189.124 Y=124.221 Z=0
    g166: GeomPoint X=185.124 Y=120.221 Z=0
    g167: Circle CenterX=175.022 CenterY=124.221 CenterZ=0 NormalX=0 NormalY=0 NormalZ=1 AngleXU=0 Radius=1
    g168: Circle CenterX=179.022 CenterY=124.221 CenterZ=0 NormalX=0 NormalY=0 NormalZ=1 AngleXU=0 Radius=1
    g169: Circle CenterX=179.022 CenterY=120.221 CenterZ=0 NormalX=0 NormalY=0 NormalZ=1 AngleXU=0 Radius=1
    g170: BSplineCurve PolesCount=3 KnotsCount=2 Degree=2 IsPeriodic=0
    g171: GeomPoint X=175.022 Y=124.221 Z=0
    g172: GeomPoint X=179.022 Y=120.221 Z=0
    g173: Circle CenterX=62.0728 CenterY=124.221 CenterZ=0 NormalX=0 NormalY=0 NormalZ=1 AngleXU=0 Radius=1
    g174: Circle CenterX=58.0728 CenterY=124.221 CenterZ=0 NormalX=0 NormalY=0 NormalZ=1 AngleXU=0 Radius=1
    g175: Circle CenterX=61.1496 CenterY=121.665 CenterZ=0 NormalX=0 NormalY=0 NormalZ=1 AngleXU=0 Radius=1
    g176: BSplineCurve PolesCount=3 KnotsCount=2 Degree=2 IsPeriodic=0
    g177: GeomPoint X=62.0728 Y=124.221 Z=0
    g178: GeomPoint X=61.1496 Y=121.665 Z=0
    g179: LineSegment StartX=62.0728 StartY=124.221 StartZ=0 EndX=175.022 EndY=124.221 EndZ=0
    g180: LineSegment StartX=179.022 StartY=120.221 StartZ=0 EndX=179.022 EndY=27.0628 EndZ=0
    g181: LineSegment StartX=185.124 StartY=27.0628 StartZ=0 EndX=185.124 EndY=120.221 EndZ=0
    g182: LineSegment StartX=189.124 StartY=124.221 StartZ=0 EndX=302.073 EndY=124.221 EndZ=0
    g183: LineSegment StartX=302.996 StartY=121.665 StartZ=0 EndX=189.124 EndY=27.0628 EndZ=0
    g184: LineSegment StartX=175.022 StartY=27.0628 StartZ=0 EndX=61.1496 EndY=121.665 EndZ=0
    g185: Circle CenterX=61.5791 CenterY=75.4095 CenterZ=0 NormalX=0 NormalY=0 NormalZ=1 AngleXU=0 Radius=1
    g186: Circle CenterX=58.0728 CenterY=77.3346 CenterZ=0 NormalX=0 NormalY=0 NormalZ=1 AngleXU=0 Radius=1
    g187: Circle CenterX=58.0728 CenterY=73.3346 CenterZ=0 NormalX=0 NormalY=0 NormalZ=1 AngleXU=0 Radius=1
    g188: BSplineCurve PolesCount=3 KnotsCount=2 Degree=2 IsPeriodic=0
    g189: GeomPoint X=61.5791 Y=75.4095 Z=0
    g190: GeomPoint X=58.0728 Y=73.3346 Z=0
    g191: Circle CenterX=58.0728 CenterY=-40.8935 CenterZ=0 NormalX=0 NormalY=0 NormalZ=1 AngleXU=0 Radius=1
    g192: Circle CenterX=58.0728 CenterY=-44.8935 CenterZ=0 NormalX=0 NormalY=0 NormalZ=1 AngleXU=0 Radius=1
    g193: Circle CenterX=61.5791 CenterY=-42.9683 CenterZ=0 NormalX=0 NormalY=0 NormalZ=1 AngleXU=0 Radius=1
    g194: BSplineCurve PolesCount=3 KnotsCount=2 Degree=2 IsPeriodic=0
    g195: GeomPoint X=58.0728 Y=-40.8935 Z=0
    g196: GeomPoint X=61.5791 Y=-42.9683 Z=0
    g197: LineSegment StartX=61.5791 StartY=-42.9683 StartZ=0 EndX=165.871 EndY=14.2954 EndZ=0
    g198: LineSegment StartX=165.871 StartY=18.1458 StartZ=0 EndX=61.5791 EndY=75.4095 EndZ=0
    g199: LineSegment StartX=58.0728 StartY=73.3346 StartZ=0 EndX=58.0728 EndY=-40.8935 EndZ=0
    g200: Circle CenterX=302.567 CenterY=-42.9683 CenterZ=0 NormalX=0 NormalY=0 NormalZ=1 AngleXU=0 Radius=1
    g201: Circle CenterX=306.073 CenterY=-44.8935 CenterZ=0 NormalX=0 NormalY=0 NormalZ=1 AngleXU=0 Radius=1
    g202: Circle CenterX=306.073 CenterY=-40.8935 CenterZ=0 NormalX=0 NormalY=0 NormalZ=1 AngleXU=0 Radius=1
    g203: BSplineCurve PolesCount=3 KnotsCount=2 Degree=2 IsPeriodic=0
    g204: GeomPoint X=302.567 Y=-42.9683 Z=0
    g205: GeomPoint X=306.073 Y=-40.8935 Z=0
    g206: Circle CenterX=306.073 CenterY=73.3346 CenterZ=0 NormalX=0 NormalY=0 NormalZ=1 AngleXU=0 Radius=1
    g207: Circle CenterX=306.073 CenterY=77.3346 CenterZ=0 NormalX=0 NormalY=0 NormalZ=1 AngleXU=0 Radius=1
    g208: Circle CenterX=302.567 CenterY=75.4095 CenterZ=0 NormalX=0 NormalY=0 NormalZ=1 AngleXU=0 Radius=1
    g209: BSplineCurve PolesCount=3 KnotsCount=2 Degree=2 IsPeriodic=0
    g210: GeomPoint X=306.073 Y=73.3346 Z=0
    g211: GeomPoint X=302.567 Y=75.4095 Z=0
    g212: LineSegment StartX=302.567 StartY=-42.9683 StartZ=0 EndX=198.275 EndY=14.2954 EndZ=0
    g213: LineSegment StartX=198.275 StartY=18.1458 StartZ=0 EndX=302.567 EndY=75.4095 EndZ=0
    g214: LineSegment StartX=306.073 StartY=73.3346 StartZ=0 EndX=306.073 EndY=-40.8935 EndZ=0
    g215: LineSegment StartX=322.073 StartY=105.865 StartZ=0 EndX=328.643 EndY=105.865 EndZ=0
    g216: LineSegment StartX=318.073 StartY=120.221 StartZ=0 EndX=318.073 EndY=109.865 EndZ=0
    g217: LineSegment StartX=336.157 StartY=107.779 StartZ=0 EndX=362.567 EndY=122.294 EndZ=0
    g218: Circle CenterX=362.073 CenterY=124.221 CenterZ=0 NormalX=0 NormalY=0 NormalZ=1 AngleXU=0 Radius=1
    g219: Circle CenterX=366.073 CenterY=124.221 CenterZ=0 NormalX=0 NormalY=0 NormalZ=1 AngleXU=0 Radius=1
    g220: Circle CenterX=362.567 CenterY=122.294 CenterZ=0 NormalX=0 NormalY=0 NormalZ=1 AngleXU=0 Radius=1
    g221: BSplineCurve PolesCount=3 KnotsCount=2 Degree=2 IsPeriodic=0
    g222: GeomPoint X=362.073 Y=124.221 Z=0
    g223: GeomPoint X=362.567 Y=122.294 Z=0
    g224: Circle CenterX=322.073 CenterY=124.221 CenterZ=0 NormalX=0 NormalY=0 NormalZ=1 AngleXU=0 Radius=1
    g225: Circle CenterX=318.073 CenterY=124.221 CenterZ=0 NormalX=0 NormalY=0 NormalZ=1 AngleXU=0 Radius=1
    g226: Circle CenterX=318.073 CenterY=120.221 CenterZ=0 NormalX=0 NormalY=0 NormalZ=1 AngleXU=0 Radius=1
    g227: BSplineCurve PolesCount=3 KnotsCount=2 Degree=2 IsPeriodic=0
    g228: GeomPoint X=322.073 Y=124.221 Z=0
    g229: GeomPoint X=318.073 Y=120.221 Z=0
    g230: Circle CenterX=322.073 CenterY=105.865 CenterZ=0 NormalX=0 NormalY=0 NormalZ=1 AngleXU=0 Radius=1
    g231: Circle CenterX=318.073 CenterY=105.865 CenterZ=0 NormalX=0 NormalY=0 NormalZ=1 AngleXU=0 Radius=1
    g232: Circle CenterX=318.073 CenterY=109.865 CenterZ=0 NormalX=0 NormalY=0 NormalZ=1 AngleXU=0 Radius=1
    g233: BSplineCurve PolesCount=3 KnotsCount=2 Degree=2 IsPeriodic=0
    g234: GeomPoint X=322.073 Y=105.865 Z=0
    g235: GeomPoint X=318.073 Y=109.865 Z=0
    g236: Circle CenterX=336.157 CenterY=107.779 CenterZ=0 NormalX=0 NormalY=0 NormalZ=1 AngleXU=0 Radius=1
    g237: Circle CenterX=332.651 CenterY=105.853 CenterZ=0 NormalX=0 NormalY=0 NormalZ=1 AngleXU=0 Radius=1
    g238: Circle CenterX=328.643 CenterY=105.865 CenterZ=0 NormalX=0 NormalY=0 NormalZ=1 AngleXU=0 Radius=1
    g239: BSplineCurve PolesCount=3 KnotsCount=2 Degree=2 IsPeriodic=0
    g240: GeomPoint X=336.157 Y=107.779 Z=0
    g241: GeomPoint X=328.643 Y=105.865 Z=0
    g242: LineSegment StartX=322.073 StartY=124.221 StartZ=0 EndX=362.073 EndY=124.221 EndZ=0
    g243: Circle CenterX=371.567 CenterY=-80.8644 CenterZ=0 NormalX=0 NormalY=0 NormalZ=1 AngleXU=0 Radius=1
    g244: Circle CenterX=375.073 CenterY=-82.7896 CenterZ=0 NormalX=0 NormalY=0 NormalZ=1 AngleXU=0 Radius=1
    g245: Circle CenterX=375.073 CenterY=-78.7896 CenterZ=0 NormalX=0 NormalY=0 NormalZ=1 AngleXU=0 Radius=1
    g246: BSplineCurve PolesCount=3 KnotsCount=2 Degree=2 IsPeriodic=0
    g247: GeomPoint X=371.567 Y=-80.8644 Z=0
    g248: GeomPoint X=375.073 Y=-78.7896 Z=0
    g249: Circle CenterX=321.579 CenterY=-53.4075 CenterZ=0 NormalX=0 NormalY=0 NormalZ=1 AngleXU=0 Radius=1
    g250: Circle CenterX=318.073 CenterY=-51.4823 CenterZ=0 NormalX=0 NormalY=0 NormalZ=1 AngleXU=0 Radius=1
    g251: Circle CenterX=318.073 CenterY=-47.4805 CenterZ=0 NormalX=0 NormalY=0 NormalZ=1 AngleXU=0 Radius=1
    g252: BSplineCurve PolesCount=3 KnotsCount=2 Degree=2 IsPeriodic=0
    g253: GeomPoint X=321.579 Y=-53.4075 Z=0
    g254: GeomPoint X=318.073 Y=-47.4805 Z=0
    g255: LineSegment StartX=371.567 StartY=-80.8644 StartZ=0 EndX=321.579 EndY=-53.4075 EndZ=0
    g256: Circle CenterX=321.579 CenterY=-67.3492 CenterZ=0 NormalX=0 NormalY=0 NormalZ=1 AngleXU=0 Radius=1
    g257: Circle CenterX=318.073 CenterY=-65.424 CenterZ=0 NormalX=0 NormalY=0 NormalZ=1 AngleXU=0 Radius=1
    g258: Circle CenterX=318.073 CenterY=-69.424 CenterZ=0 NormalX=0 NormalY=0 NormalZ=1 AngleXU=0 Radius=1
    g259: BSplineCurve PolesCount=3 KnotsCount=2 Degree=2 IsPeriodic=0
    g260: GeomPoint X=321.579 Y=-67.3492 Z=0
    g261: GeomPoint X=318.073 Y=-69.424 Z=0
    g262: Circle CenterX=362.567 CenterY=-89.8542 CenterZ=0 NormalX=0 NormalY=0 NormalZ=1 AngleXU=0 Radius=1
    g263: Circle CenterX=366.073 CenterY=-91.7794 CenterZ=0 NormalX=0 NormalY=0 NormalZ=1 AngleXU=0 Radius=1
    g264: Circle CenterX=362.073 CenterY=-91.7794 CenterZ=0 NormalX=0 NormalY=0 NormalZ=1 AngleXU=0 Radius=1
    g265: BSplineCurve PolesCount=3 KnotsCount=2 Degree=2 IsPeriodic=0
    g266: GeomPoint X=362.567 Y=-89.8542 Z=0
    g267: GeomPoint X=362.073 Y=-91.7794 Z=0
    g268: Circle CenterX=322.073 CenterY=-91.7794 CenterZ=0 NormalX=0 NormalY=0 NormalZ=1 AngleXU=0 Radius=1
    g269: Circle CenterX=318.073 CenterY=-91.7794 CenterZ=0 NormalX=0 NormalY=0 NormalZ=1 AngleXU=0 Radius=1
    g270: Circle CenterX=318.073 CenterY=-87.7794 CenterZ=0 NormalX=0 NormalY=0 NormalZ=1 AngleXU=0 Radius=1
    g271: BSplineCurve PolesCount=3 KnotsCount=2 Degree=2 IsPeriodic=0
    g272: GeomPoint X=322.073 Y=-91.7794 Z=0
    g273: GeomPoint X=318.073 Y=-87.7794 Z=0
    g274: LineSegment StartX=362.567 StartY=-89.8542 StartZ=0 EndX=321.579 EndY=-67.3492 EndZ=0
    g275: LineSegment StartX=318.073 StartY=-69.424 StartZ=0 EndX=318.073 EndY=-87.7794 EndZ=0
    g276: LineSegment StartX=322.073 StartY=-91.7794 StartZ=0 EndX=362.073 EndY=-91.7794 EndZ=0
    g277: Circle CenterX=2.07281 CenterY=124.221 CenterZ=0 NormalX=0 NormalY=0 NormalZ=1 AngleXU=0 Radius=1
    g278: Circle CenterX=1.57905 CenterY=122.295 CenterZ=0 NormalX=0 NormalY=0 NormalZ=1 AngleXU=0 Radius=1
    g279: BSplineCurve PolesCount=3 KnotsCount=2 Degree=2 IsPeriodic=0
    g280: GeomPoint X=2.07281 Y=124.221 Z=0
    g281: GeomPoint X=1.57905 Y=122.295 Z=0
    g282: Circle CenterX=42.0728 CenterY=124.221 CenterZ=0 NormalX=0 NormalY=0 NormalZ=1 AngleXU=0 Radius=1
    g283: Circle CenterX=46.0728 CenterY=124.221 CenterZ=0 NormalX=0 NormalY=0 NormalZ=1 AngleXU=0 Radius=1
    g284: Circle CenterX=46.0728 CenterY=120.221 CenterZ=0 NormalX=0 NormalY=0 NormalZ=1 AngleXU=0 Radius=1
    g285: BSplineCurve PolesCount=3 KnotsCount=2 Degree=2 IsPeriodic=0
    g286: GeomPoint X=42.0728 Y=124.221 Z=0
    g287: GeomPoint X=46.0728 Y=120.221 Z=0
    g288: Circle CenterX=46.0728 CenterY=109.865 CenterZ=0 NormalX=0 NormalY=0 NormalZ=1 AngleXU=0 Radius=1
    g289: Circle CenterX=46.0728 CenterY=105.865 CenterZ=0 NormalX=0 NormalY=0 NormalZ=1 AngleXU=0 Radius=1
    g290: Circle CenterX=42.0728 CenterY=105.865 CenterZ=0 NormalX=0 NormalY=0 NormalZ=1 AngleXU=0 Radius=1
    g291: BSplineCurve PolesCount=3 KnotsCount=2 Degree=2 IsPeriodic=0
    g292: GeomPoint X=46.0728 Y=109.865 Z=0
    g293: GeomPoint X=42.0728 Y=105.865 Z=0
    g294: Circle CenterX=35.5028 CenterY=105.865 CenterZ=0 NormalX=0 NormalY=0 NormalZ=1 AngleXU=0 Radius=1
    g295: Circle CenterX=31.5028 CenterY=105.865 CenterZ=0 NormalX=0 NormalY=0 NormalZ=1 AngleXU=0 Radius=1
    g296: Circle CenterX=27.9965 CenterY=107.79 CenterZ=0 NormalX=0 NormalY=0 NormalZ=1 AngleXU=0 Radius=1
    g297: BSplineCurve PolesCount=3 KnotsCount=2 Degree=2 IsPeriodic=0
    g298: GeomPoint X=35.5028 Y=105.865 Z=0
    g299: GeomPoint X=27.9965 Y=107.79 Z=0
    g300: LineSegment StartX=2.07281 StartY=124.221 StartZ=0 EndX=42.0728 EndY=124.221 EndZ=0
    g301: LineSegment StartX=46.0728 StartY=120.221 StartZ=0 EndX=46.0728 EndY=109.865 EndZ=0
    g302: LineSegment StartX=42.0728 StartY=105.865 StartZ=0 EndX=35.5028 EndY=105.865 EndZ=0
    g303: LineSegment StartX=27.9965 StartY=107.79 StartZ=0 EndX=1.57905 EndY=122.295 EndZ=0
    g304: Circle CenterX=42.5666 CenterY=-67.3492 CenterZ=0 NormalX=0 NormalY=0 NormalZ=1 AngleXU=0 Radius=1
    g305: Circle CenterX=46.0728 CenterY=-65.424 CenterZ=0 NormalX=0 NormalY=0 NormalZ=1 AngleXU=0 Radius=1
    g306: Circle CenterX=46.0728 CenterY=-69.424 CenterZ=0 NormalX=0 NormalY=0 NormalZ=1 AngleXU=0 Radius=1
    g307: BSplineCurve PolesCount=3 KnotsCount=2 Degree=2 IsPeriodic=0
    g308: GeomPoint X=42.5666 Y=-67.3492 Z=0
    g309: GeomPoint X=46.0728 Y=-69.424 Z=0
    g310: Circle CenterX=46.0728 CenterY=-87.7794 CenterZ=0 NormalX=0 NormalY=0 NormalZ=1 AngleXU=0 Radius=1
    g311: Circle CenterX=46.0728 CenterY=-91.7794 CenterZ=0 NormalX=0 NormalY=0 NormalZ=1 AngleXU=0 Radius=1
    g312: Circle CenterX=42.0728 CenterY=-91.7794 CenterZ=0 NormalX=0 NormalY=0 NormalZ=1 AngleXU=0 Radius=1
    g313: BSplineCurve PolesCount=3 KnotsCount=2 Degree=2 IsPeriodic=0
    g314: GeomPoint X=46.0728 Y=-87.7794 Z=0
    g315: GeomPoint X=42.0728 Y=-91.7794 Z=0
    g316: Circle CenterX=2.07281 CenterY=-91.7794 CenterZ=0 NormalX=0 NormalY=0 NormalZ=1 AngleXU=0 Radius=1
    g317: Circle CenterX=-1.92719 CenterY=-91.7794 CenterZ=0 NormalX=0 NormalY=0 NormalZ=1 AngleXU=0 Radius=1
    g318: Circle CenterX=1.57905 CenterY=-89.8542 CenterZ=0 NormalX=0 NormalY=0 NormalZ=1 AngleXU=0 Radius=1
    g319: BSplineCurve PolesCount=3 KnotsCount=2 Degree=2 IsPeriodic=0
    g320: GeomPoint X=2.07281 Y=-91.7794 Z=0
    g321: GeomPoint X=1.57905 Y=-89.8542 Z=0
    g322: LineSegment StartX=2.07281 StartY=-91.7794 StartZ=0 EndX=42.0728 EndY=-91.7794 EndZ=0
    g323: LineSegment StartX=46.0728 StartY=-87.7794 StartZ=0 EndX=46.0728 EndY=-69.424 EndZ=0
    g324: LineSegment StartX=42.5666 StartY=-67.3492 StartZ=0 EndX=1.57905 EndY=-89.8542 EndZ=0
    g325: Circle CenterX=322.073 CenterY=76.4095 CenterZ=0 NormalX=0 NormalY=0 NormalZ=1 AngleXU=0 Radius=4
    g326: BSplineCurve PolesCount=3 KnotsCount=2 Degree=2 IsPeriodic=0
    g327: GeomPoint X=318.073 Y=72.4095 Z=0
    g328: GeomPoint X=322.073 Y=76.4095 Z=0
    g329: Circle CenterX=375.073 CenterY=72.4095 CenterZ=0 NormalX=0 NormalY=0 NormalZ=1 AngleXU=0 Radius=1
    g330: Circle CenterX=375.073 CenterY=76.4095 CenterZ=0 NormalX=0 NormalY=0 NormalZ=1 AngleXU=0 Radius=1
    g331: Circle CenterX=371.073 CenterY=76.4095 CenterZ=0 NormalX=0 NormalY=0 NormalZ=1 AngleXU=0 Radius=1
    g332: BSplineCurve PolesCount=3 KnotsCount=2 Degree=2 IsPeriodic=0
    g333: GeomPoint X=375.073 Y=72.4095 Z=0
    g334: GeomPoint X=371.073 Y=76.4095 Z=0
    g335: LineSegment StartX=322.073 StartY=76.4095 StartZ=0 EndX=371.073 EndY=76.4095 EndZ=0
    g336: LineSegment StartX=318.073 StartY=72.4095 StartZ=0 EndX=318.073 EndY=-47.4805 EndZ=0
    g337: LineSegment StartX=375.073 StartY=72.4095 StartZ=0 EndX=375.073 EndY=-78.7896 EndZ=0
    g338: ArcOfCircle CenterX=-26.9272 CenterY=22.1087 CenterZ=0 NormalX=0 NormalY=0 NormalZ=1 AngleXU=0 Radius=4 StartAngle=5e-16 EndAngle=3.14159
    g339: LineSegment StartX=-22.9272 StartY=22.1087 StartZ=0 EndX=-18.9272 EndY=-83.7794 EndZ=0
    g340: LineSegment StartX=-34.9272 StartY=-83.7794 StartZ=0 EndX=-30.9272 EndY=22.1087 EndZ=0
    g341: ArcOfCircle CenterX=391.073 CenterY=22.1087 CenterZ=0 NormalX=0 NormalY=0 NormalZ=1 AngleXU=0 Radius=4 StartAngle=0 EndAngle=3.14159
    g342: LineSegment StartX=387.073 StartY=22.1087 StartZ=0 EndX=383.073 EndY=-83.7794 EndZ=0
    g343: LineSegment StartX=395.073 StartY=22.1087 StartZ=0 EndX=399.073 EndY=-83.7794 EndZ=0
    g344: Circle CenterX=-10.9272 CenterY=-78.7794 CenterZ=0 NormalX=0 NormalY=0 NormalZ=1 AngleXU=0 Radius=1
    g345: Circle CenterX=-10.9272 CenterY=-82.7794 CenterZ=0 NormalX=0 NormalY=0 NormalZ=1 AngleXU=0 Radius=1
    g346: Circle CenterX=-7.42095 CenterY=-80.8542 CenterZ=0 NormalX=0 NormalY=0 NormalZ=1 AngleXU=0 Radius=1
    g347: BSplineCurve PolesCount=3 KnotsCount=2 Degree=2 IsPeriodic=0
    g348: GeomPoint X=-10.9272 Y=-78.7794 Z=0
    g349: GeomPoint X=-7.42095 Y=-80.8542 Z=0
    g350: Circle CenterX=42.5666 CenterY=-53.4075 CenterZ=0 NormalX=0 NormalY=0 NormalZ=1 AngleXU=0 Radius=1
    g351: Circle CenterX=46.0728 CenterY=-51.4823 CenterZ=0 NormalX=0 NormalY=0 NormalZ=1 AngleXU=0 Radius=1
    g352: Circle CenterX=46.0728 CenterY=-47.4823 CenterZ=0 NormalX=0 NormalY=0 NormalZ=1 AngleXU=0 Radius=1
    g353: BSplineCurve PolesCount=3 KnotsCount=2 Degree=2 IsPeriodic=0
    g354: GeomPoint X=42.5666 Y=-53.4075 Z=0
    g355: GeomPoint X=46.0728 Y=-47.4823 Z=0
    g356: Circle CenterX=46.0728 CenterY=72.4095 CenterZ=0 NormalX=0 NormalY=0 NormalZ=1 AngleXU=0 Radius=1
    g357: Circle CenterX=46.0728 CenterY=76.4095 CenterZ=0 NormalX=0 NormalY=0 NormalZ=1 AngleXU=0 Radius=1
    g358: Circle CenterX=42.0728 CenterY=76.4095 CenterZ=0 NormalX=0 NormalY=0 NormalZ=1 AngleXU=0 Radius=1
    g359: BSplineCurve PolesCount=3 KnotsCount=2 Degree=2 IsPeriodic=0
    g360: GeomPoint X=46.0728 Y=72.4095 Z=0
    g361: GeomPoint X=42.0728 Y=76.4095 Z=0
    g362: Circle CenterX=-6.92718 CenterY=76.4095 CenterZ=0 NormalX=0 NormalY=0 NormalZ=1 AngleXU=0 Radius=1
    g363: Circle CenterX=-10.9272 CenterY=76.4095 CenterZ=0 NormalX=0 NormalY=0 NormalZ=1 AngleXU=0 Radius=1
    g364: Circle CenterX=-10.9272 CenterY=72.4095 CenterZ=0 NormalX=0 NormalY=0 NormalZ=1 AngleXU=0 Radius=1
    g365: BSplineCurve PolesCount=3 KnotsCount=2 Degree=2 IsPeriodic=0
    g366: GeomPoint X=-6.92718 Y=76.4095 Z=0
    g367: GeomPoint X=-10.9272 Y=72.4095 Z=0
    g368: LineSegment StartX=-10.9272 StartY=72.4095 StartZ=0 EndX=-10.9272 EndY=-78.7794 EndZ=0
    g369: LineSegment StartX=-7.42095 StartY=-80.8542 StartZ=0 EndX=42.5666 EndY=-53.4075 EndZ=0
    g370: LineSegment StartX=46.0728 StartY=-47.4823 StartZ=0 EndX=46.0728 EndY=72.4095 EndZ=0
    g371: LineSegment StartX=42.0728 StartY=76.4095 StartZ=0 EndX=-6.92719 EndY=76.4095 EndZ=0
    g372: LineSegment StartX=232.072 StartY=136.221 StartZ=0 EndX=232.072 EndY=-117.815 EndZ=0
    g373: LineSegment StartX=132.072 StartY=136.221 StartZ=0 EndX=132.072 EndY=-121.309 EndZ=0
    g374: LineSegment StartX=245.072 StartY=136.221 StartZ=0 EndX=245.072 EndY=-116.499 EndZ=0
    g375: LineSegment StartX=119.072 StartY=136.221 StartZ=0 EndX=119.072 EndY=-116.228 EndZ=0
    g376: LineSegment StartX=-42.9272 StartY=136.221 StartZ=0 EndX=407.073 EndY=136.221 EndZ=0
  constraints (624):
    c: Vertical(g0)
    c: Vertical(g1)
    c: Block(g1)
    c: Block(g0)
    c: Weight(g4) = 1
    c: Equal(g4,g5)
    c: Equal(g4,g6)
    c: InternalAlignment(g4,g7)
    c: InternalAlignment(g5,g7)
    c: InternalAlignment(g6,g7)
    c: InternalAlignment(g8,g7)
    c: InternalAlignment(g9,g7)
    c: Weight(g10) = 1
    c: Equal(g10,g11)
    c: Equal(g10,g12)
    c: InternalAlignment(g10,g13)
    c: InternalAlignment(g11,g13)
    c: InternalAlignment(g12,g13)
    c: InternalAlignment(g14,g13)
    c: InternalAlignment(g15,g13)
    c: Block(g13)
    c: Block(g7)
    c: Weight(g16) = 1
    c: Equal(g16,g17)
    c: Equal(g16,g18)
    c: InternalAlignment(g16,g19)
    c: InternalAlignment(g17,g19)
    c: InternalAlignment(g18,g19)
    c: InternalAlignment(g20,g19)
    c: InternalAlignment(g21,g19)
    c: Weight(g22) = 1
    c: Equal(g22,g23)
    c: Equal(g22,g24)
    c: InternalAlignment(g22,g25)
    c: InternalAlignment(g23,g25)
    c: InternalAlignment(g24,g25)
    c: InternalAlignment(g26,g25)
    c: InternalAlignment(g27,g25)
    c: Block(g25)
    c: Block(g19)
    c: Weight(g28) = 1
    c: Equal(g28,g29)
    c: Equal(g28,g30)
    c: InternalAlignment(g28,g31)
    c: InternalAlignment(g29,g31)
    c: InternalAlignment(g30,g31)
    c: InternalAlignment(g32,g31)
    c: InternalAlignment(g33,g31)
    c: Weight(g34) = 1
    c: Equal(g34,g35)
    c: Equal(g34,g36)
    c: InternalAlignment(g34,g37)
    c: InternalAlignment(g35,g37)
    c: InternalAlignment(g36,g37)
    c: InternalAlignment(g38,g37)
    c: InternalAlignment(g39,g37)
    c: Block(g31)
    c: Block(g37)
    c: Coincident(g40,g1)
    c: Coincident(g40,g0)
    c: Horizontal(g40)
    c: Distance(g40) = 450
    c: Weight(g41) = 1
    c: Equal(g41,g42)
    c: Equal(g41,g43)
    c: InternalAlignment(g41,g44)
    c: InternalAlignment(g42,g44)
    c: InternalAlignment(g43,g44)
    c: InternalAlignment(g45,g44)
    c: InternalAlignment(g46,g44)
    c: Block(g44)
    c: Weight(g47) = 1
    c: Equal(g47,g48)
    c: Equal(g47,g49)
    c: InternalAlignment(g47,g50)
    c: InternalAlignment(g48,g50)
    c: InternalAlignment(g49,g50)
    c: InternalAlignment(g51,g50)
    c: InternalAlignment(g52,g50)
    c: Block(g50)
    c: Weight(g53) = 1
    c: Equal(g53,g54)
    c: Equal(g53,g55)
    c: InternalAlignment(g53,g56)
    c: InternalAlignment(g54,g56)
    c: InternalAlignment(g55,g56)
    c: InternalAlignment(g57,g56)
    c: InternalAlignment(g58,g56)
    c: Block(g56)
    c: Weight(g59) = 1
    c: Equal(g59,g60)
    c: Equal(g59,g61)
    c: InternalAlignment(g59,g62)
    c: InternalAlignment(g60,g62)
    c: InternalAlignment(g61,g62)
    c: InternalAlignment(g63,g62)
    c: InternalAlignment(g64,g62)
    c: Block(g62)
    c: Weight(g65) = 1
    c: Equal(g65,g66)
    c: Equal(g65,g67)
    c: InternalAlignment(g65,g68)
    c: InternalAlignment(g66,g68)
    c: InternalAlignment(g67,g68)
    c: InternalAlignment(g69,g68)
    c: InternalAlignment(g70,g68)
    c: Weight(g71) = 1
    c: Equal(g71,g72)
    c: Equal(g71,g73)
    c: InternalAlignment(g71,g74)
    c: InternalAlignment(g72,g74)
    c: InternalAlignment(g73,g74)
    c: InternalAlignment(g75,g74)
    c: InternalAlignment(g76,g74)
    c: Block(g68)
    c: Block(g74)
    c: Coincident(g77,g68)
    c: Coincident(g77,g74)
    c: Vertical(g77)
    c: Coincident(g78,g68)
    c: Coincident(g78,g50)
    c: Coincident(g79,g50)
    c: Coincident(g79,g74)
    c: Weight(g80) = 1
    c: Equal(g80,g81)
    c: Equal(g80,g82)
    c: InternalAlignment(g80,g83)
    c: InternalAlignment(g81,g83)
    c: InternalAlignment(g82,g83)
    c: InternalAlignment(g84,g83)
    c: InternalAlignment(g85,g83)
    c: Weight(g86) = 1
    c: Equal(g86,g87)
    c: Equal(g86,g88)
    c: InternalAlignment(g86,g89)
    c: InternalAlignment(g87,g89)
    c: InternalAlignment(g88,g89)
    c: InternalAlignment(g90,g89)
    c: InternalAlignment(g91,g89)
    c: Block(g83)
    c: Block(g89)
    c: Coincident(g92,g83)
    c: Coincident(g92,g89)
    c: Vertical(g92)
    c: Coincident(g93,g83)
    c: Coincident(g93,g44)
    c: Coincident(g94,g44)
    c: Coincident(g94,g89)
    c: Weight(g95) = 1
    c: Equal(g95,g96)
    c: Equal(g95,g97)
    c: InternalAlignment(g95,g98)
    c: InternalAlignment(g96,g98)
    c: InternalAlignment(g97,g98)
    c: InternalAlignment(g99,g98)
    c: InternalAlignment(g100,g98)
    c: Weight(g101) = 1
    c: Equal(g101,g102)
    c: Equal(g101,g103)
    c: InternalAlignment(g101,g104)
    c: InternalAlignment(g102,g104)
    c: InternalAlignment(g103,g104)
    c: InternalAlignment(g105,g104)
    c: InternalAlignment(g106,g104)
    c: Block(g98)
    c: Block(g104)
    c: Coincident(g107,g98)
    c: Coincident(g107,g104)
    c: Vertical(g107)
    c: Coincident(g108,g104)
    c: Coincident(g108,g62)
    c: Coincident(g109,g62)
    c: Coincident(g109,g98)
    c: Weight(g110) = 1
    c: Equal(g110,g111)
    c: Equal(g110,g112)
    c: InternalAlignment(g110,g113)
    c: InternalAlignment(g111,g113)
    c: InternalAlignment(g112,g113)
    c: InternalAlignment(g114,g113)
    c: InternalAlignment(g115,g113)
    c: Weight(g116) = 1
    c: Equal(g116,g117)
    c: Equal(g116,g118)
    c: InternalAlignment(g116,g119)
    c: InternalAlignment(g117,g119)
    c: InternalAlignment(g118,g119)
    c: InternalAlignment(g120,g119)
    c: InternalAlignment(g121,g119)
    c: Block(g113)
    c: Block(g119)
    c: Coincident(g122,g113)
    c: Coincident(g122,g119)
    c: Vertical(g122)
    c: Coincident(g123,g119)
    c: Coincident(g123,g56)
    c: Coincident(g124,g56)
    c: Coincident(g124,g113)
    c: Weight(g125) = 1
    c: Equal(g125,g126)
    c: Equal(g125,g127)
    c: InternalAlignment(g125,g128)
    c: InternalAlignment(g126,g128)
    c: InternalAlignment(g127,g128)
    c: InternalAlignment(g129,g128)
    c: InternalAlignment(g130,g128)
    c: Weight(g131) = 1
    c: Equal(g131,g132)
    c: Equal(g131,g133)
    c: InternalAlignment(g131,g134)
    c: InternalAlignment(g132,g134)
    c: InternalAlignment(g133,g134)
    c: InternalAlignment(g135,g134)
    c: InternalAlignment(g136,g134)
    c: Weight(g137) = 1
    c: Equal(g137,g138)
    c: Equal(g137,g139)
    c: InternalAlignment(g137,g140)
    c: InternalAlignment(g138,g140)
    c: InternalAlignment(g139,g140)
    c: InternalAlignment(g141,g140)
    c: InternalAlignment(g142,g140)
    c: Weight(g143) = 1
    c: Equal(g143,g144)
    c: Equal(g143,g145)
    c: InternalAlignment(g143,g146)
    c: InternalAlignment(g144,g146)
    c: InternalAlignment(g145,g146)
    c: InternalAlignment(g147,g146)
    c: InternalAlignment(g148,g146)
    c: Block(g146)
    c: Block(g140)
    c: Block(g134)
    c: Block(g128)
    c: Coincident(g149,g25)
    c: Coincident(g149,g146)
    c: Coincident(g150,g146)
    c: Coincident(g150,g140)
    c: Horizontal(g150)
    c: Coincident(g151,g140)
    c: Coincident(g151,g25)
    c: Vertical(g151)
    c: Coincident(g152,g19)
    c: Coincident(g152,g134)
    c: Vertical(g152)
    c: Coincident(g153,g134)
    c: Coincident(g153,g128)
    c: Horizontal(g153)
    c: Coincident(g154,g128)
    c: Coincident(g154,g19)
    c: Weight(g155) = 1
    c: Equal(g155,g156)
    c: Equal(g155,g157)
    c: InternalAlignment(g155,g158)
    c: InternalAlignment(g156,g158)
    c: InternalAlignment(g157,g158)
    c: InternalAlignment(g159,g158)
    c: InternalAlignment(g160,g158)
    c: Weight(g161) = 1
    c: Equal(g161,g162)
    c: Equal(g161,g163)
    c: InternalAlignment(g161,g164)
    c: InternalAlignment(g162,g164)
    c: InternalAlignment(g163,g164)
    c: InternalAlignment(g165,g164)
    c: InternalAlignment(g166,g164)
    c: Weight(g167) = 1
    c: Equal(g167,g168)
    c: Equal(g167,g169)
    c: InternalAlignment(g167,g170)
    c: InternalAlignment(g168,g170)
    c: InternalAlignment(g169,g170)
    c: InternalAlignment(g171,g170)
    c: InternalAlignment(g172,g170)
    c: Weight(g173) = 1
    c: Equal(g173,g174)
    c: Equal(g173,g175)
    c: InternalAlignment(g173,g176)
    c: InternalAlignment(g174,g176)
    c: InternalAlignment(g175,g176)
    c: InternalAlignment(g177,g176)
    c: InternalAlignment(g178,g176)
    c: Block(g176)
    c: Block(g170)
    c: Block(g164)
    c: Block(g158)
    c: Coincident(g179,g176)
    c: Coincident(g179,g170)
    c: Horizontal(g179)
    c: Coincident(g180,g170)
    c: Coincident(g180,g7)
    c: Vertical(g180)
    c: Coincident(g181,g13)
    c: Coincident(g181,g164)
    c: Vertical(g181)
    c: Coincident(g182,g164)
    c: Coincident(g182,g158)
    c: Horizontal(g182)
    c: Coincident(g183,g158)
    c: Coincident(g183,g13)
    c: Coincident(g184,g7)
    c: Weight(g185) = 1
    c: Equal(g185,g186)
    c: Equal(g185,g187)
    c: InternalAlignment(g185,g188)
    c: InternalAlignment(g186,g188)
    c: InternalAlignment(g187,g188)
    c: InternalAlignment(g189,g188)
    c: InternalAlignment(g190,g188)
    c: Weight(g191) = 1
    c: Equal(g191,g192)
    c: Equal(g191,g193)
    c: InternalAlignment(g191,g194)
    c: InternalAlignment(g192,g194)
    c: InternalAlignment(g193,g194)
    c: InternalAlignment(g195,g194)
    c: InternalAlignment(g196,g194)
    c: Block(g194)
    c: Block(g188)
    c: Coincident(g197,g194)
    c: Coincident(g197,g31)
    c: Coincident(g198,g31)
    c: Coincident(g198,g188)
    c: Coincident(g199,g188)
    c: Coincident(g199,g194)
    c: Vertical(g199)
    c: Weight(g200) = 1
    c: Equal(g200,g201)
    c: Equal(g200,g202)
    c: InternalAlignment(g200,g203)
    c: InternalAlignment(g201,g203)
    c: InternalAlignment(g202,g203)
    c: InternalAlignment(g204,g203)
    c: InternalAlignment(g205,g203)
    c: Weight(g206) = 1
    c: Equal(g206,g207)
    c: Equal(g206,g208)
    c: InternalAlignment(g206,g209)
    c: InternalAlignment(g207,g209)
    c: InternalAlignment(g208,g209)
    c: InternalAlignment(g210,g209)
    c: InternalAlignment(g211,g209)
    c: Block(g209)
    c: Block(g203)
    c: Coincident(g212,g203)
    c: Coincident(g212,g37)
    c: Coincident(g213,g37)
    c: Coincident(g213,g209)
    c: Coincident(g214,g209)
    c: Coincident(g214,g203)
    c: Vertical(g214)
    c: Horizontal(g215)
    c: Block(g215)
    c: Vertical(g216)
    c: Block(g216)
    c: Block(g217)
    c: Weight(g218) = 1
    c: Equal(g218,g219)
    c: Equal(g218,g220)
    c: InternalAlignment(g218,g221)
    c: InternalAlignment(g219,g221)
    c: InternalAlignment(g220,g221)
    c: InternalAlignment(g222,g221)
    c: InternalAlignment(g223,g221)
    c: Weight(g224) = 1
    c: Equal(g224,g225)
    c: Equal(g224,g226)
    c: InternalAlignment(g224,g227)
    c: InternalAlignment(g225,g227)
    c: InternalAlignment(g226,g227)
    c: InternalAlignment(g228,g227)
    c: InternalAlignment(g229,g227)
    c: Weight(g230) = 1
    c: Equal(g230,g231)
    c: Equal(g230,g232)
    c: InternalAlignment(g230,g233)
    c: InternalAlignment(g231,g233)
    c: InternalAlignment(g232,g233)
    c: InternalAlignment(g234,g233)
    c: InternalAlignment(g235,g233)
    c: Weight(g236) = 1
    c: Equal(g236,g237)
    c: Equal(g236,g238)
    c: InternalAlignment(g236,g239)
    c: InternalAlignment(g237,g239)
    c: InternalAlignment(g238,g239)
    c: InternalAlignment(g240,g239)
    c: InternalAlignment(g241,g239)
    c: Block(g221)
    c: Block(g227)
    c: Block(g233)
    c: Block(g239)
    c: Coincident(g242,g227)
    c: Coincident(g242,g221)
    c: Horizontal(g242)
    c: Block(g184)
    c: Weight(g243) = 1
    c: Equal(g243,g244)
    c: Equal(g243,g245)
    c: InternalAlignment(g243,g246)
    c: InternalAlignment(g244,g246)
    c: InternalAlignment(g245,g246)
    c: InternalAlignment(g247,g246)
    c: InternalAlignment(g248,g246)
    c: Weight(g249) = 1
    c: Equal(g249,g250)
    c: Equal(g249,g251)
    c: InternalAlignment(g249,g252)
    c: InternalAlignment(g250,g252)
    c: InternalAlignment(g251,g252)
    c: InternalAlignment(g253,g252)
    c: InternalAlignment(g254,g252)
    c: Block(g246)
    c: Block(g252)
    c: Coincident(g255,g246)
    c: Coincident(g255,g252)
    c: Weight(g256) = 1
    c: Equal(g256,g257)
    c: Equal(g256,g258)
    c: InternalAlignment(g256,g259)
    c: InternalAlignment(g257,g259)
    c: InternalAlignment(g258,g259)
    c: InternalAlignment(g260,g259)
    c: InternalAlignment(g261,g259)
    c: Weight(g262) = 1
    c: Equal(g262,g263)
    c: Equal(g262,g264)
    c: InternalAlignment(g262,g265)
    c: InternalAlignment(g263,g265)
    c: InternalAlignment(g264,g265)
    c: InternalAlignment(g266,g265)
    c: InternalAlignment(g267,g265)
    c: Weight(g268) = 1
    c: Equal(g268,g269)
    c: Equal(g268,g270)
    c: InternalAlignment(g268,g271)
    c: InternalAlignment(g269,g271)
    c: InternalAlignment(g270,g271)
    c: InternalAlignment(g272,g271)
    c: InternalAlignment(g273,g271)
    c: Block(g271)
    c: Block(g265)
    c: Block(g259)
    c: Coincident(g274,g265)
    c: Coincident(g274,g259)
    c: Coincident(g275,g259)
    c: Coincident(g275,g271)
    c: Vertical(g275)
    c: Coincident(g276,g271)
    c: Coincident(g276,g265)
    c: Horizontal(g276)
    c: Weight(g277) = 1
    c: Equal(g277,g278)
    c: InternalAlignment(g277,g279)
    c: InternalAlignment(g278,g279)
    c: InternalAlignment(g280,g279)
    c: InternalAlignment(g281,g279)
    c: Weight(g282) = 1
    c: InternalAlignment(g283,g285)
    c: InternalAlignment(g284,g285)
    c: InternalAlignment(g286,g285)
    c: InternalAlignment(g287,g285)
    c: Weight(g288) = 1
    c: Equal(g288,g289)
    c: Equal(g288,g290)
    c: InternalAlignment(g288,g291)
    c: InternalAlignment(g289,g291)
    c: InternalAlignment(g290,g291)
    c: InternalAlignment(g292,g291)
    c: InternalAlignment(g293,g291)
    c: Equal(g294,g295)
    c: Equal(g294,g296)
    c: InternalAlignment(g294,g297)
    c: InternalAlignment(g295,g297)
    c: InternalAlignment(g296,g297)
    c: InternalAlignment(g298,g297)
    c: InternalAlignment(g299,g297)
    c: Block(g285)
    c: Block(g291)
    c: Block(g297)
    c: Block(g279)
    c: Coincident(g300,g279)
    c: Coincident(g300,g285)
    c: Horizontal(g300)
    c: Coincident(g301,g285)
    c: Coincident(g301,g291)
    c: Vertical(g301)
    c: Coincident(g302,g291)
    c: Coincident(g302,g297)
    c: Horizontal(g302)
    c: Coincident(g303,g297)
    c: Coincident(g303,g279)
    c: Weight(g304) = 1
    c: Equal(g304,g305)
    c: Equal(g304,g306)
    c: InternalAlignment(g304,g307)
    c: InternalAlignment(g305,g307)
    c: InternalAlignment(g306,g307)
    c: InternalAlignment(g308,g307)
    c: InternalAlignment(g309,g307)
    c: Weight(g310) = 1
    c: Equal(g310,g311)
    c: Equal(g310,g312)
    c: InternalAlignment(g310,g313)
    c: InternalAlignment(g311,g313)
    c: InternalAlignment(g312,g313)
    c: InternalAlignment(g314,g313)
    c: InternalAlignment(g315,g313)
    c: Weight(g316) = 1
    c: Equal(g316,g317)
    c: Equal(g316,g318)
    c: InternalAlignment(g316,g319)
    c: InternalAlignment(g317,g319)
    c: InternalAlignment(g318,g319)
    c: InternalAlignment(g320,g319)
    c: InternalAlignment(g321,g319)
    c: Block(g319)
    c: Block(g313)
    c: Block(g307)
    c: Coincident(g322,g319)
    c: Coincident(g322,g313)
    c: Horizontal(g322)
    c: Coincident(g323,g313)
    c: Coincident(g323,g307)
    c: Vertical(g323)
    c: Coincident(g324,g307)
    c: Coincident(g324,g319)
    c: InternalAlignment(g325,g326)
    c: InternalAlignment(g327,g326)
    c: InternalAlignment(g328,g326)
    c: Block(g326)
    c: Equal(g329,g330)
    c: Equal(g329,g331)
    c: InternalAlignment(g329,g332)
    c: InternalAlignment(g330,g332)
    c: InternalAlignment(g331,g332)
    c: InternalAlignment(g333,g332)
    c: InternalAlignment(g334,g332)
    c: Block(g332)
    c: Coincident(g335,g326)
    c: Horizontal(g335)
    c: Block(g335)
    c: Coincident(g336,g326)
    c: Coincident(g336,g252)
    c: Vertical(g336)
    c: Coincident(g337,g332)
    c: Coincident(g337,g246)
    c: Vertical(g337)
    c: Block(g338)
    c: Block(g2)
    c: Distance(g336) = 119.89
    c: Coincident(g339,g338)
    c: Coincident(g339,g2)
    c: Coincident(g340,g2)
    c: Coincident(g340,g338)
    c: Block(g3)
    c: Block(g341)
    c: Coincident(g342,g341)
    c: Coincident(g342,g3)
    c: Coincident(g343,g341)
    c: Coincident(g343,g3)
    c: Block(g343)
    c: Block(g342)
    c: Weight(g344) = 1
    c: Equal(g344,g345)
    c: Equal(g344,g346)
    c: InternalAlignment(g344,g347)
    c: InternalAlignment(g345,g347)
    c: InternalAlignment(g346,g347)
    c: InternalAlignment(g348,g347)
    c: InternalAlignment(g349,g347)
    c: Weight(g350) = 1
    c: Equal(g350,g351)
    c: Equal(g350,g352)
    c: InternalAlignment(g350,g353)
    c: InternalAlignment(g351,g353)
    c: InternalAlignment(g352,g353)
    c: InternalAlignment(g354,g353)
    c: InternalAlignment(g355,g353)
    c: Weight(g356) = 1
    c: Equal(g356,g357)
    c: Equal(g356,g358)
    c: InternalAlignment(g356,g359)
    c: InternalAlignment(g357,g359)
    c: InternalAlignment(g358,g359)
    c: InternalAlignment(g360,g359)
    c: InternalAlignment(g361,g359)
    c: Weight(g362) = 1
    c: Equal(g362,g363)
    c: Equal(g362,g364)
    c: InternalAlignment(g362,g365)
    c: InternalAlignment(g363,g365)
    c: InternalAlignment(g364,g365)
    c: InternalAlignment(g366,g365)
    c: InternalAlignment(g367,g365)
    c: Block(g365)
    c: Block(g359)
    c: Block(g353)
    c: Block(g347)
    c: Coincident(g368,g365)
    c: Coincident(g368,g347)
    c: Vertical(g368)
    c: Coincident(g369,g347)
    c: Coincident(g369,g353)
    c: Coincident(g370,g353)
    c: Coincident(g370,g359)
    c: Vertical(g370)
    c: Coincident(g371,g359)
    c: Coincident(g371,g365)
    c: Horizontal(g371)
    c: Vertical(g372)
    c: Vertical(g373)
    c: Vertical(g374)
    c: Vertical(g375)
    c: Coincident(g376,g0)
    c: Coincident(g376,g1)
    c: Horizontal(g376)
    c: Block(g376)
    c: Distance(g376) = 450
    c: Block(g374)
    c: Block(g372)
    c: Block(g373)
    c: Block(g375)
    c: Distance(g0) = 240
FEATURE [Part::Extrusion] Extrude005
  Base = -> Sketch003
  Dir = (0,0,1)
  DirMode = 2
  FaceMakerClass = Part::FaceMakerBullseye
  LengthFwd = 24
  LengthRev = 0
  Solid = true
  Symmetric = false
